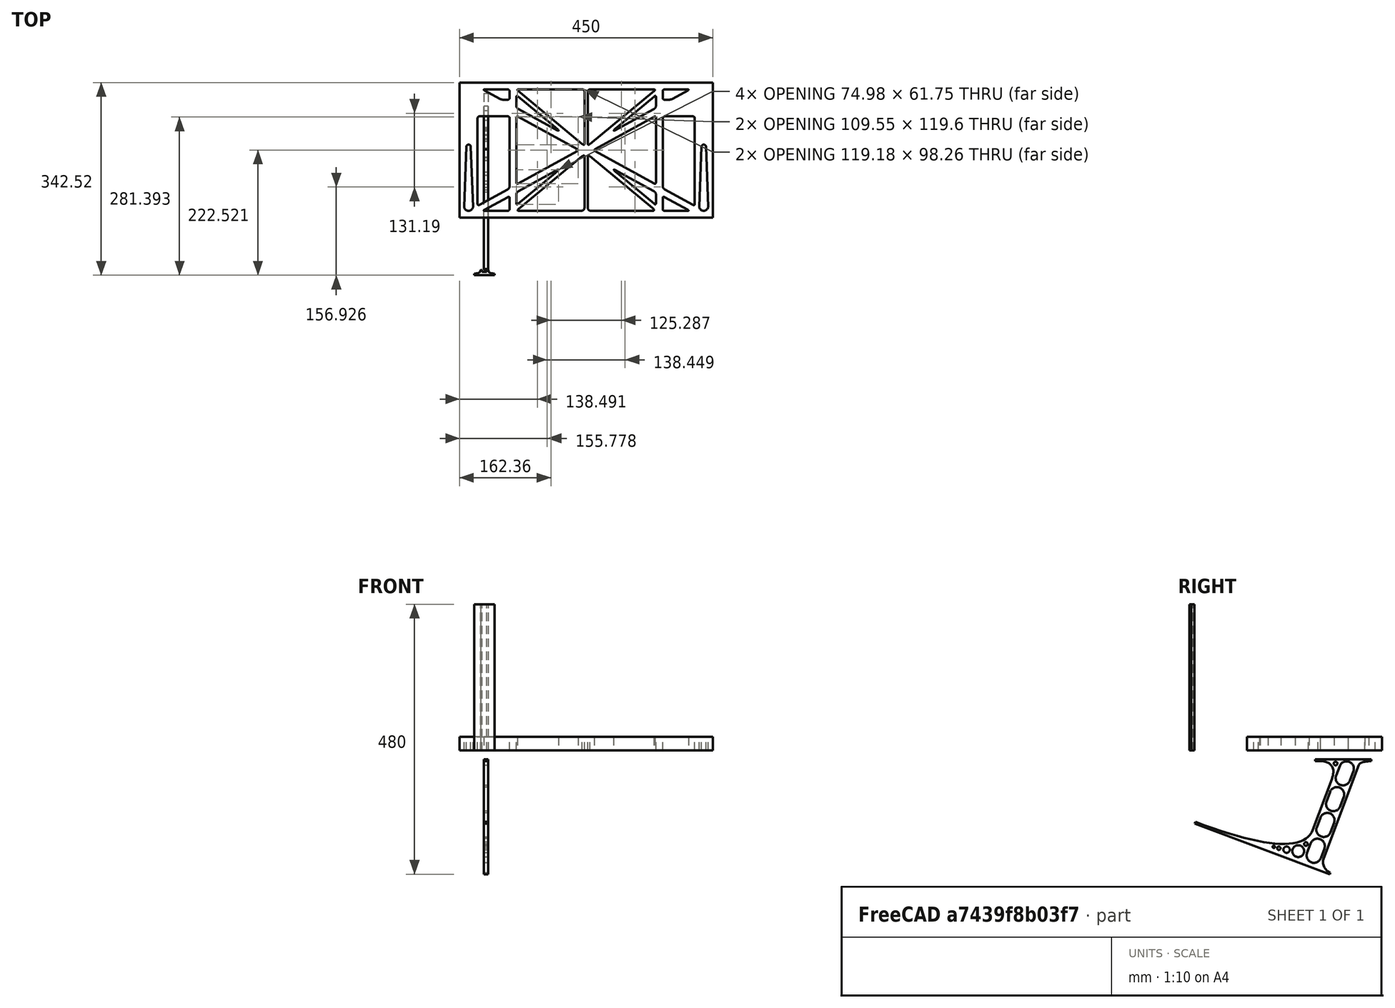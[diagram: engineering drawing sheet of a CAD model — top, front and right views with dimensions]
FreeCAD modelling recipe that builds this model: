
FCSTD DOCUMENT  (FreeCAD 0.19R0.19.2)
Label: laptopStand160FCStd
License: All rights reserved
LicenseURL: http://en.wikipedia.org/wiki/All_rights_reserved
objects: Sketcher::SketchObject×4, Part::Extrusion×3
note: 7 computed .brp shape members not serialized (recipe doc carries the construction recipe); baked Part::Feature solids carry a one-line shape summary decoded from their .brp

FEATURE [Sketcher::SketchObject] Sketch
  FullyConstrained = false
  sketch-geometry (349):
    g0: LineSegment StartX=-10.9272 StartY=-82.7794 StartZ=0 EndX=46.0728 EndY=-51.4823 EndZ=0
    g1: LineSegment StartX=-10.9272 StartY=76.4095 StartZ=0 EndX=-10.9272 EndY=-82.7794 EndZ=0
    g2: LineSegment StartX=46.0728 StartY=76.4095 StartZ=0 EndX=46.0728 EndY=-51.4823 EndZ=0
    g3: LineSegment StartX=-42.9272 StartY=136.221 StartZ=0 EndX=-42.9272 EndY=-103.779 EndZ=0
    g4: LineSegment StartX=407.073 StartY=136.221 StartZ=0 EndX=407.073 EndY=-103.779 EndZ=0
    g5: ArcOfCircle CenterX=-26.9272 CenterY=-83.7794 CenterZ=0 NormalX=0 NormalY=0 NormalZ=1 AngleXU=0 Radius=8 StartAngle=3.14159 EndAngle=6.28319
    g6: ArcOfCircle CenterX=391.073 CenterY=22.1087 CenterZ=0 NormalX=0 NormalY=0 NormalZ=1 AngleXU=0 Radius=8 StartAngle=-4.4e-15 EndAngle=3.14159
    g7: LineSegment StartX=399.073 StartY=22.1087 StartZ=0 EndX=399.073 EndY=-83.7794 EndZ=0
    g8: LineSegment StartX=383.073 StartY=22.1087 StartZ=0 EndX=383.073 EndY=-83.7794 EndZ=0
    g9: ArcOfCircle CenterX=391.073 CenterY=-83.7794 CenterZ=0 NormalX=0 NormalY=0 NormalZ=1 AngleXU=0 Radius=8 StartAngle=3.14159 EndAngle=6.28319
    g10: Circle CenterX=175.022 CenterY=27.0628 CenterZ=0 NormalX=0 NormalY=0 NormalZ=1 AngleXU=0 Radius=1
    g11: Circle CenterX=179.022 CenterY=24.8665 CenterZ=0 NormalX=0 NormalY=0 NormalZ=1 AngleXU=0 Radius=1
    g12: Circle CenterX=179.022 CenterY=27.0628 CenterZ=0 NormalX=0 NormalY=0 NormalZ=1 AngleXU=0 Radius=1
    g13: BSplineCurve PolesCount=3 KnotsCount=2 Degree=2 IsPeriodic=0
    g14: GeomPoint X=175.022 Y=27.0628 Z=0
    g15: GeomPoint X=179.022 Y=27.0628 Z=0
    g16: Circle CenterX=189.124 CenterY=27.0628 CenterZ=0 NormalX=0 NormalY=0 NormalZ=1 AngleXU=0 Radius=1
    g17: Circle CenterX=185.124 CenterY=24.8665 CenterZ=0 NormalX=0 NormalY=0 NormalZ=1 AngleXU=0 Radius=1
    g18: Circle CenterX=185.124 CenterY=27.0628 CenterZ=0 NormalX=0 NormalY=0 NormalZ=1 AngleXU=0 Radius=1
    g19: BSplineCurve PolesCount=3 KnotsCount=2 Degree=2 IsPeriodic=0
    g20: GeomPoint X=189.124 Y=27.0628 Z=0
    g21: GeomPoint X=185.124 Y=27.0628 Z=0
    g22: Circle CenterX=175.022 CenterY=5.37834 CenterZ=0 NormalX=0 NormalY=0 NormalZ=1 AngleXU=0 Radius=1
    g23: Circle CenterX=179.022 CenterY=7.57463 CenterZ=0 NormalX=0 NormalY=0 NormalZ=1 AngleXU=0 Radius=1
    g24: Circle CenterX=179.022 CenterY=5.34704 CenterZ=0 NormalX=0 NormalY=0 NormalZ=1 AngleXU=0 Radius=1
    g25: BSplineCurve PolesCount=3 KnotsCount=2 Degree=2 IsPeriodic=0
    g26: GeomPoint X=175.022 Y=5.37834 Z=0
    g27: GeomPoint X=179.022 Y=5.34704 Z=0
    g28: Circle CenterX=189.124 CenterY=5.37834 CenterZ=0 NormalX=0 NormalY=0 NormalZ=1 AngleXU=0 Radius=1
    g29: Circle CenterX=185.124 CenterY=7.57463 CenterZ=0 NormalX=0 NormalY=0 NormalZ=1 AngleXU=0 Radius=1
    g30: Circle CenterX=185.124 CenterY=5.34704 CenterZ=0 NormalX=0 NormalY=0 NormalZ=1 AngleXU=0 Radius=1
    g31: BSplineCurve PolesCount=3 KnotsCount=2 Degree=2 IsPeriodic=0
    g32: GeomPoint X=189.124 Y=5.37834 Z=0
    g33: GeomPoint X=185.124 Y=5.34704 Z=0
    g34: Circle CenterX=165.871 CenterY=18.1458 CenterZ=0 NormalX=0 NormalY=0 NormalZ=1 AngleXU=0 Radius=1
    g35: Circle CenterX=169.377 CenterY=16.2206 CenterZ=0 NormalX=0 NormalY=0 NormalZ=1 AngleXU=0 Radius=1
    g36: Circle CenterX=165.871 CenterY=14.2954 CenterZ=0 NormalX=0 NormalY=0 NormalZ=1 AngleXU=0 Radius=1
    g37: BSplineCurve PolesCount=3 KnotsCount=2 Degree=2 IsPeriodic=0
    g38: GeomPoint X=165.871 Y=18.1458 Z=0
    g39: GeomPoint X=165.871 Y=14.2954 Z=0
    g40: Circle CenterX=198.275 CenterY=18.1458 CenterZ=0 NormalX=0 NormalY=0 NormalZ=1 AngleXU=0 Radius=1
    g41: Circle CenterX=194.768 CenterY=16.2206 CenterZ=0 NormalX=0 NormalY=0 NormalZ=1 AngleXU=0 Radius=1
    g42: Circle CenterX=198.275 CenterY=14.2954 CenterZ=0 NormalX=0 NormalY=0 NormalZ=1 AngleXU=0 Radius=1
    g43: BSplineCurve PolesCount=3 KnotsCount=2 Degree=2 IsPeriodic=0
    g44: GeomPoint X=198.275 Y=18.1458 Z=0
    g45: GeomPoint X=198.275 Y=14.2954 Z=0
    g46: LineSegment StartX=407.073 StartY=-103.779 StartZ=0 EndX=-42.9272 EndY=-103.779 EndZ=0
    g47: LineSegment StartX=407.073 StartY=136.221 StartZ=0 EndX=-42.9272 EndY=136.221 EndZ=0
    g48: LineSegment StartX=46.0728 StartY=76.4095 StartZ=0 EndX=-10.9272 EndY=76.4095 EndZ=0
    g49: Circle CenterX=125.607 CenterY=54.1951 CenterZ=0 NormalX=0 NormalY=0 NormalZ=1 AngleXU=0 Radius=1
    g50: Circle CenterX=139.632 CenterY=46.4944 CenterZ=0 NormalX=0 NormalY=0 NormalZ=1 AngleXU=0 Radius=1
    g51: Circle CenterX=127.326 CenterY=56.7187 CenterZ=0 NormalX=0 NormalY=0 NormalZ=1 AngleXU=0 Radius=1
    g52: BSplineCurve PolesCount=3 KnotsCount=2 Degree=2 IsPeriodic=0
    g53: GeomPoint X=125.607 Y=54.1951 Z=0
    g54: GeomPoint X=127.326 Y=56.7187 Z=0
    g55: Circle CenterX=236.821 CenterY=56.7187 CenterZ=0 NormalX=0 NormalY=0 NormalZ=1 AngleXU=0 Radius=1
    g56: Circle CenterX=224.513 CenterY=46.4944 CenterZ=0 NormalX=0 NormalY=0 NormalZ=1 AngleXU=0 Radius=1
    g57: Circle CenterX=238.538 CenterY=54.1951 CenterZ=0 NormalX=0 NormalY=0 NormalZ=1 AngleXU=0 Radius=1
    g58: BSplineCurve PolesCount=3 KnotsCount=2 Degree=2 IsPeriodic=0
    g59: GeomPoint X=236.821 Y=56.7187 Z=0
    g60: GeomPoint X=238.538 Y=54.1951 Z=0
    g61: Circle CenterX=238.538 CenterY=-21.7539 CenterZ=0 NormalX=0 NormalY=0 NormalZ=1 AngleXU=0 Radius=1
    g62: Circle CenterX=224.513 CenterY=-14.0532 CenterZ=0 NormalX=0 NormalY=0 NormalZ=1 AngleXU=0 Radius=1
    g63: Circle CenterX=236.821 CenterY=-24.2775 CenterZ=0 NormalX=0 NormalY=0 NormalZ=1 AngleXU=0 Radius=1
    g64: BSplineCurve PolesCount=3 KnotsCount=2 Degree=2 IsPeriodic=0
    g65: GeomPoint X=238.538 Y=-21.7539 Z=0
    g66: GeomPoint X=236.821 Y=-24.2775 Z=0
    g67: Circle CenterX=125.607 CenterY=-21.7539 CenterZ=0 NormalX=0 NormalY=0 NormalZ=1 AngleXU=0 Radius=1
    g68: Circle CenterX=139.632 CenterY=-14.0532 CenterZ=0 NormalX=0 NormalY=0 NormalZ=1 AngleXU=0 Radius=1
    g69: Circle CenterX=127.325 CenterY=-24.2775 CenterZ=0 NormalX=0 NormalY=0 NormalZ=1 AngleXU=0 Radius=1
    g70: BSplineCurve PolesCount=3 KnotsCount=2 Degree=2 IsPeriodic=0
    g71: GeomPoint X=125.607 Y=-21.7539 Z=0
    g72: GeomPoint X=127.325 Y=-24.2775 Z=0
    g73: Circle CenterX=302.996 CenterY=111.695 CenterZ=0 NormalX=0 NormalY=0 NormalZ=1 AngleXU=0 Radius=1
    g74: Circle CenterX=306.073 CenterY=114.251 CenterZ=0 NormalX=0 NormalY=0 NormalZ=1 AngleXU=0 Radius=1
    g75: Circle CenterX=306.073 CenterY=110.251 CenterZ=0 NormalX=0 NormalY=0 NormalZ=1 AngleXU=0 Radius=1
    g76: BSplineCurve PolesCount=3 KnotsCount=2 Degree=2 IsPeriodic=0
    g77: GeomPoint X=302.996 Y=111.695 Z=0
    g78: GeomPoint X=306.073 Y=110.251 Z=0
    g79: Circle CenterX=306.073 CenterY=95.2763 CenterZ=0 NormalX=0 NormalY=0 NormalZ=1 AngleXU=0 Radius=1
    g80: Circle CenterX=306.073 CenterY=91.2763 CenterZ=0 NormalX=0 NormalY=0 NormalZ=1 AngleXU=0 Radius=1
    g81: Circle CenterX=302.567 CenterY=89.3511 CenterZ=0 NormalX=0 NormalY=0 NormalZ=1 AngleXU=0 Radius=1
    g82: BSplineCurve PolesCount=3 KnotsCount=2 Degree=2 IsPeriodic=0
    g83: GeomPoint X=306.073 Y=95.2763 Z=0
    g84: GeomPoint X=302.567 Y=89.3511 Z=0
    g85: LineSegment StartX=306.073 StartY=110.251 StartZ=0 EndX=306.073 EndY=95.2763 EndZ=0
    g86: LineSegment StartX=302.996 StartY=111.695 StartZ=0 EndX=236.821 EndY=56.7187 EndZ=0
    g87: LineSegment StartX=238.538 StartY=54.1951 StartZ=0 EndX=302.567 EndY=89.3511 EndZ=0
    g88: Circle CenterX=61.1496 CenterY=111.695 CenterZ=0 NormalX=0 NormalY=0 NormalZ=1 AngleXU=0 Radius=1
    g89: Circle CenterX=58.0728 CenterY=114.251 CenterZ=0 NormalX=0 NormalY=0 NormalZ=1 AngleXU=0 Radius=1
    g90: Circle CenterX=58.0728 CenterY=110.251 CenterZ=0 NormalX=0 NormalY=0 NormalZ=1 AngleXU=0 Radius=1
    g91: BSplineCurve PolesCount=3 KnotsCount=2 Degree=2 IsPeriodic=0
    g92: GeomPoint X=61.1496 Y=111.695 Z=0
    g93: GeomPoint X=58.0728 Y=110.251 Z=0
    g94: Circle CenterX=61.5791 CenterY=89.3511 CenterZ=0 NormalX=0 NormalY=0 NormalZ=1 AngleXU=0 Radius=1
    g95: Circle CenterX=58.0728 CenterY=91.2763 CenterZ=0 NormalX=0 NormalY=0 NormalZ=1 AngleXU=0 Radius=1
    g96: Circle CenterX=58.0728 CenterY=95.2763 CenterZ=0 NormalX=0 NormalY=0 NormalZ=1 AngleXU=0 Radius=1
    g97: BSplineCurve PolesCount=3 KnotsCount=2 Degree=2 IsPeriodic=0
    g98: GeomPoint X=61.5791 Y=89.3511 Z=0
    g99: GeomPoint X=58.0728 Y=95.2763 Z=0
    g100: LineSegment StartX=58.0728 StartY=110.251 StartZ=0 EndX=58.0728 EndY=95.2763 EndZ=0
    g101: LineSegment StartX=61.1496 StartY=111.695 StartZ=0 EndX=127.326 EndY=56.7187 EndZ=0
    g102: LineSegment StartX=125.607 StartY=54.1951 StartZ=0 EndX=61.5791 EndY=89.3511 EndZ=0
    g103: Circle CenterX=61.5791 CenterY=-56.9099 CenterZ=0 NormalX=0 NormalY=0 NormalZ=1 AngleXU=0 Radius=1
    g104: Circle CenterX=58.0728 CenterY=-58.8351 CenterZ=0 NormalX=0 NormalY=0 NormalZ=1 AngleXU=0 Radius=1
    g105: Circle CenterX=58.0728 CenterY=-62.8351 CenterZ=0 NormalX=0 NormalY=0 NormalZ=1 AngleXU=0 Radius=1
    g106: BSplineCurve PolesCount=3 KnotsCount=2 Degree=2 IsPeriodic=0
    g107: GeomPoint X=61.5791 Y=-56.9099 Z=0
    g108: GeomPoint X=58.0728 Y=-62.8351 Z=0
    g109: Circle CenterX=58.0728 CenterY=-77.8102 CenterZ=0 NormalX=0 NormalY=0 NormalZ=1 AngleXU=0 Radius=1
    g110: Circle CenterX=58.0728 CenterY=-81.8102 CenterZ=0 NormalX=0 NormalY=0 NormalZ=1 AngleXU=0 Radius=1
    g111: Circle CenterX=61.1496 CenterY=-79.2541 CenterZ=0 NormalX=0 NormalY=0 NormalZ=1 AngleXU=0 Radius=1
    g112: BSplineCurve PolesCount=3 KnotsCount=2 Degree=2 IsPeriodic=0
    g113: GeomPoint X=58.0728 Y=-77.8102 Z=0
    g114: GeomPoint X=61.1496 Y=-79.2541 Z=0
    g115: LineSegment StartX=58.0728 StartY=-62.8351 StartZ=0 EndX=58.0728 EndY=-77.8102 EndZ=0
    g116: LineSegment StartX=61.1496 StartY=-79.2541 StartZ=0 EndX=127.325 EndY=-24.2775 EndZ=0
    g117: LineSegment StartX=125.607 StartY=-21.7539 StartZ=0 EndX=61.5791 EndY=-56.9099 EndZ=0
    g118: Circle CenterX=302.567 CenterY=-56.9099 CenterZ=0 NormalX=0 NormalY=0 NormalZ=1 AngleXU=0 Radius=1
    g119: Circle CenterX=306.073 CenterY=-58.8351 CenterZ=0 NormalX=0 NormalY=0 NormalZ=1 AngleXU=0 Radius=1
    g120: Circle CenterX=306.073 CenterY=-62.8351 CenterZ=0 NormalX=0 NormalY=0 NormalZ=1 AngleXU=0 Radius=1
    g121: BSplineCurve PolesCount=3 KnotsCount=2 Degree=2 IsPeriodic=0
    g122: GeomPoint X=302.567 Y=-56.9099 Z=0
    g123: GeomPoint X=306.073 Y=-62.8351 Z=0
    g124: Circle CenterX=302.996 CenterY=-79.2541 CenterZ=0 NormalX=0 NormalY=0 NormalZ=1 AngleXU=0 Radius=1
    g125: Circle CenterX=306.073 CenterY=-81.8102 CenterZ=0 NormalX=0 NormalY=0 NormalZ=1 AngleXU=0 Radius=1
    g126: Circle CenterX=306.073 CenterY=-77.8102 CenterZ=0 NormalX=0 NormalY=0 NormalZ=1 AngleXU=0 Radius=1
    g127: BSplineCurve PolesCount=3 KnotsCount=2 Degree=2 IsPeriodic=0
    g128: GeomPoint X=302.996 Y=-79.2541 Z=0
    g129: GeomPoint X=306.073 Y=-77.8102 Z=0
    g130: LineSegment StartX=306.073 StartY=-62.8351 StartZ=0 EndX=306.073 EndY=-77.8102 EndZ=0
    g131: LineSegment StartX=302.996 StartY=-79.2541 StartZ=0 EndX=236.821 EndY=-24.2775 EndZ=0
    g132: LineSegment StartX=238.538 StartY=-21.7539 StartZ=0 EndX=302.567 EndY=-56.9099 EndZ=0
    g133: Circle CenterX=61.6457 CenterY=-88.8112 CenterZ=0 NormalX=0 NormalY=0 NormalZ=1 AngleXU=0 Radius=1
    g134: Circle CenterX=58.0728 CenterY=-91.7794 CenterZ=0 NormalX=0 NormalY=0 NormalZ=1 AngleXU=0 Radius=1
    g135: Circle CenterX=63.9135 CenterY=-91.7794 CenterZ=0 NormalX=0 NormalY=0 NormalZ=1 AngleXU=0 Radius=1
    g136: BSplineCurve PolesCount=3 KnotsCount=2 Degree=2 IsPeriodic=0
    g137: GeomPoint X=61.6457 Y=-88.8112 Z=0
    g138: GeomPoint X=63.9135 Y=-91.7794 Z=0
    g139: Circle CenterX=179.022 CenterY=-85.8163 CenterZ=0 NormalX=0 NormalY=0 NormalZ=1 AngleXU=0 Radius=1
    g140: Circle CenterX=179.022 CenterY=-91.7794 CenterZ=0 NormalX=0 NormalY=0 NormalZ=1 AngleXU=0 Radius=1
    g141: Circle CenterX=171.895 CenterY=-91.7794 CenterZ=0 NormalX=0 NormalY=0 NormalZ=1 AngleXU=0 Radius=1
    g142: BSplineCurve PolesCount=3 KnotsCount=2 Degree=2 IsPeriodic=0
    g143: GeomPoint X=179.022 Y=-85.8163 Z=0
    g144: GeomPoint X=171.895 Y=-91.7794 Z=0
    g145: Circle CenterX=185.124 CenterY=-86.2028 CenterZ=0 NormalX=0 NormalY=0 NormalZ=1 AngleXU=0 Radius=1
    g146: Circle CenterX=185.124 CenterY=-91.7794 CenterZ=0 NormalX=0 NormalY=0 NormalZ=1 AngleXU=0 Radius=1
    g147: Circle CenterX=191.747 CenterY=-91.7794 CenterZ=0 NormalX=0 NormalY=0 NormalZ=1 AngleXU=0 Radius=1
    g148: BSplineCurve PolesCount=3 KnotsCount=2 Degree=2 IsPeriodic=0
    g149: GeomPoint X=185.124 Y=-86.2028 Z=0
    g150: GeomPoint X=191.747 Y=-91.7794 Z=0
    g151: Circle CenterX=299.888 CenterY=-86.6413 CenterZ=0 NormalX=0 NormalY=0 NormalZ=1 AngleXU=0 Radius=1
    g152: Circle CenterX=306.073 CenterY=-91.7794 CenterZ=0 NormalX=0 NormalY=0 NormalZ=1 AngleXU=0 Radius=1
    g153: Circle CenterX=298.776 CenterY=-91.7794 CenterZ=0 NormalX=0 NormalY=0 NormalZ=1 AngleXU=0 Radius=1
    g154: BSplineCurve PolesCount=3 KnotsCount=2 Degree=2 IsPeriodic=0
    g155: GeomPoint X=299.888 Y=-86.6413 Z=0
    g156: GeomPoint X=298.776 Y=-91.7794 Z=0
    g157: LineSegment StartX=189.124 StartY=5.37834 StartZ=0 EndX=299.888 EndY=-86.6413 EndZ=0
    g158: LineSegment StartX=298.776 StartY=-91.7794 StartZ=0 EndX=191.747 EndY=-91.7794 EndZ=0
    g159: LineSegment StartX=185.124 StartY=-86.2028 StartZ=0 EndX=185.124 EndY=5.34704 EndZ=0
    g160: LineSegment StartX=179.022 StartY=5.34704 StartZ=0 EndX=179.022 EndY=-85.8163 EndZ=0
    g161: LineSegment StartX=171.895 StartY=-91.7794 StartZ=0 EndX=63.9135 EndY=-91.7794 EndZ=0
    g162: LineSegment StartX=61.6457 StartY=-88.8112 StartZ=0 EndX=175.022 EndY=5.37834 EndZ=0
    g163: Circle CenterX=302.073 CenterY=124.221 CenterZ=0 NormalX=0 NormalY=0 NormalZ=1 AngleXU=0 Radius=1
    g164: Circle CenterX=306.073 CenterY=124.221 CenterZ=0 NormalX=0 NormalY=0 NormalZ=1 AngleXU=0 Radius=1
    g165: Circle CenterX=302.996 CenterY=121.665 CenterZ=0 NormalX=0 NormalY=0 NormalZ=1 AngleXU=0 Radius=1
    g166: BSplineCurve PolesCount=3 KnotsCount=2 Degree=2 IsPeriodic=0
    g167: GeomPoint X=302.073 Y=124.221 Z=0
    g168: GeomPoint X=302.996 Y=121.665 Z=0
    g169: Circle CenterX=189.124 CenterY=124.221 CenterZ=0 NormalX=0 NormalY=0 NormalZ=1 AngleXU=0 Radius=1
    g170: Circle CenterX=185.124 CenterY=124.221 CenterZ=0 NormalX=0 NormalY=0 NormalZ=1 AngleXU=0 Radius=1
    g171: Circle CenterX=185.124 CenterY=120.221 CenterZ=0 NormalX=0 NormalY=0 NormalZ=1 AngleXU=0 Radius=1
    g172: BSplineCurve PolesCount=3 KnotsCount=2 Degree=2 IsPeriodic=0
    g173: GeomPoint X=189.124 Y=124.221 Z=0
    g174: GeomPoint X=185.124 Y=120.221 Z=0
    g175: Circle CenterX=175.022 CenterY=124.221 CenterZ=0 NormalX=0 NormalY=0 NormalZ=1 AngleXU=0 Radius=1
    g176: Circle CenterX=179.022 CenterY=124.221 CenterZ=0 NormalX=0 NormalY=0 NormalZ=1 AngleXU=0 Radius=1
    g177: Circle CenterX=179.022 CenterY=120.221 CenterZ=0 NormalX=0 NormalY=0 NormalZ=1 AngleXU=0 Radius=1
    g178: BSplineCurve PolesCount=3 KnotsCount=2 Degree=2 IsPeriodic=0
    g179: GeomPoint X=175.022 Y=124.221 Z=0
    g180: GeomPoint X=179.022 Y=120.221 Z=0
    g181: Circle CenterX=62.0728 CenterY=124.221 CenterZ=0 NormalX=0 NormalY=0 NormalZ=1 AngleXU=0 Radius=1
    g182: Circle CenterX=58.0728 CenterY=124.221 CenterZ=0 NormalX=0 NormalY=0 NormalZ=1 AngleXU=0 Radius=1
    g183: Circle CenterX=61.1496 CenterY=121.665 CenterZ=0 NormalX=0 NormalY=0 NormalZ=1 AngleXU=0 Radius=1
    g184: BSplineCurve PolesCount=3 KnotsCount=2 Degree=2 IsPeriodic=0
    g185: GeomPoint X=62.0728 Y=124.221 Z=0
    g186: GeomPoint X=61.1496 Y=121.665 Z=0
    g187: LineSegment StartX=62.0728 StartY=124.221 StartZ=0 EndX=175.022 EndY=124.221 EndZ=0
    g188: LineSegment StartX=179.022 StartY=120.221 StartZ=0 EndX=179.022 EndY=27.0628 EndZ=0
    g189: LineSegment StartX=185.124 StartY=27.0628 StartZ=0 EndX=185.124 EndY=120.221 EndZ=0
    g190: LineSegment StartX=189.124 StartY=124.221 StartZ=0 EndX=302.073 EndY=124.221 EndZ=0
    g191: LineSegment StartX=302.996 StartY=121.665 StartZ=0 EndX=189.124 EndY=27.0628 EndZ=0
    g192: LineSegment StartX=175.022 StartY=27.0628 StartZ=0 EndX=61.1496 EndY=121.665 EndZ=0
    g193: Circle CenterX=61.5791 CenterY=75.4095 CenterZ=0 NormalX=0 NormalY=0 NormalZ=1 AngleXU=0 Radius=1
    g194: Circle CenterX=58.0728 CenterY=77.3346 CenterZ=0 NormalX=0 NormalY=0 NormalZ=1 AngleXU=0 Radius=1
    g195: Circle CenterX=58.0728 CenterY=73.3346 CenterZ=0 NormalX=0 NormalY=0 NormalZ=1 AngleXU=0 Radius=1
    g196: BSplineCurve PolesCount=3 KnotsCount=2 Degree=2 IsPeriodic=0
    g197: GeomPoint X=61.5791 Y=75.4095 Z=0
    g198: GeomPoint X=58.0728 Y=73.3346 Z=0
    g199: Circle CenterX=58.0728 CenterY=-40.8935 CenterZ=0 NormalX=0 NormalY=0 NormalZ=1 AngleXU=0 Radius=1
    g200: Circle CenterX=58.0728 CenterY=-44.8935 CenterZ=0 NormalX=0 NormalY=0 NormalZ=1 AngleXU=0 Radius=1
    g201: Circle CenterX=61.5791 CenterY=-42.9683 CenterZ=0 NormalX=0 NormalY=0 NormalZ=1 AngleXU=0 Radius=1
    g202: BSplineCurve PolesCount=3 KnotsCount=2 Degree=2 IsPeriodic=0
    g203: GeomPoint X=58.0728 Y=-40.8935 Z=0
    g204: GeomPoint X=61.5791 Y=-42.9683 Z=0
    g205: LineSegment StartX=61.5791 StartY=-42.9683 StartZ=0 EndX=165.871 EndY=14.2954 EndZ=0
    g206: LineSegment StartX=165.871 StartY=18.1458 StartZ=0 EndX=61.5791 EndY=75.4095 EndZ=0
    g207: LineSegment StartX=58.0728 StartY=73.3346 StartZ=0 EndX=58.0728 EndY=-40.8935 EndZ=0
    g208: Circle CenterX=302.567 CenterY=-42.9683 CenterZ=0 NormalX=0 NormalY=0 NormalZ=1 AngleXU=0 Radius=1
    g209: Circle CenterX=306.073 CenterY=-44.8935 CenterZ=0 NormalX=0 NormalY=0 NormalZ=1 AngleXU=0 Radius=1
    g210: Circle CenterX=306.073 CenterY=-40.8935 CenterZ=0 NormalX=0 NormalY=0 NormalZ=1 AngleXU=0 Radius=1
    g211: BSplineCurve PolesCount=3 KnotsCount=2 Degree=2 IsPeriodic=0
    g212: GeomPoint X=302.567 Y=-42.9683 Z=0
    g213: GeomPoint X=306.073 Y=-40.8935 Z=0
    g214: Circle CenterX=306.073 CenterY=73.3346 CenterZ=0 NormalX=0 NormalY=0 NormalZ=1 AngleXU=0 Radius=1
    g215: Circle CenterX=306.073 CenterY=77.3346 CenterZ=0 NormalX=0 NormalY=0 NormalZ=1 AngleXU=0 Radius=1
    g216: Circle CenterX=302.567 CenterY=75.4095 CenterZ=0 NormalX=0 NormalY=0 NormalZ=1 AngleXU=0 Radius=1
    g217: BSplineCurve PolesCount=3 KnotsCount=2 Degree=2 IsPeriodic=0
    g218: GeomPoint X=306.073 Y=73.3346 Z=0
    g219: GeomPoint X=302.567 Y=75.4095 Z=0
    g220: LineSegment StartX=302.567 StartY=-42.9683 StartZ=0 EndX=198.275 EndY=14.2954 EndZ=0
    g221: LineSegment StartX=198.275 StartY=18.1458 StartZ=0 EndX=302.567 EndY=75.4095 EndZ=0
    g222: LineSegment StartX=306.073 StartY=73.3346 StartZ=0 EndX=306.073 EndY=-40.8935 EndZ=0
    g223: LineSegment StartX=322.073 StartY=105.865 StartZ=0 EndX=328.643 EndY=105.865 EndZ=0
    g224: LineSegment StartX=318.073 StartY=120.221 StartZ=0 EndX=318.073 EndY=109.865 EndZ=0
    g225: LineSegment StartX=336.157 StartY=107.779 StartZ=0 EndX=362.567 EndY=122.294 EndZ=0
    g226: Circle CenterX=362.073 CenterY=124.221 CenterZ=0 NormalX=0 NormalY=0 NormalZ=1 AngleXU=0 Radius=1
    g227: Circle CenterX=366.073 CenterY=124.221 CenterZ=0 NormalX=0 NormalY=0 NormalZ=1 AngleXU=0 Radius=1
    g228: Circle CenterX=362.567 CenterY=122.294 CenterZ=0 NormalX=0 NormalY=0 NormalZ=1 AngleXU=0 Radius=1
    g229: BSplineCurve PolesCount=3 KnotsCount=2 Degree=2 IsPeriodic=0
    g230: GeomPoint X=362.073 Y=124.221 Z=0
    g231: GeomPoint X=362.567 Y=122.294 Z=0
    g232: Circle CenterX=322.073 CenterY=124.221 CenterZ=0 NormalX=0 NormalY=0 NormalZ=1 AngleXU=0 Radius=1
    g233: Circle CenterX=318.073 CenterY=124.221 CenterZ=0 NormalX=0 NormalY=0 NormalZ=1 AngleXU=0 Radius=1
    g234: Circle CenterX=318.073 CenterY=120.221 CenterZ=0 NormalX=0 NormalY=0 NormalZ=1 AngleXU=0 Radius=1
    g235: BSplineCurve PolesCount=3 KnotsCount=2 Degree=2 IsPeriodic=0
    g236: GeomPoint X=322.073 Y=124.221 Z=0
    g237: GeomPoint X=318.073 Y=120.221 Z=0
    g238: Circle CenterX=322.073 CenterY=105.865 CenterZ=0 NormalX=0 NormalY=0 NormalZ=1 AngleXU=0 Radius=1
    g239: Circle CenterX=318.073 CenterY=105.865 CenterZ=0 NormalX=0 NormalY=0 NormalZ=1 AngleXU=0 Radius=1
    g240: Circle CenterX=318.073 CenterY=109.865 CenterZ=0 NormalX=0 NormalY=0 NormalZ=1 AngleXU=0 Radius=1
    g241: BSplineCurve PolesCount=3 KnotsCount=2 Degree=2 IsPeriodic=0
    g242: GeomPoint X=322.073 Y=105.865 Z=0
    g243: GeomPoint X=318.073 Y=109.865 Z=0
    g244: Circle CenterX=336.157 CenterY=107.779 CenterZ=0 NormalX=0 NormalY=0 NormalZ=1 AngleXU=0 Radius=1
    g245: Circle CenterX=332.651 CenterY=105.853 CenterZ=0 NormalX=0 NormalY=0 NormalZ=1 AngleXU=0 Radius=1
    g246: Circle CenterX=328.643 CenterY=105.865 CenterZ=0 NormalX=0 NormalY=0 NormalZ=1 AngleXU=0 Radius=1
    g247: BSplineCurve PolesCount=3 KnotsCount=2 Degree=2 IsPeriodic=0
    g248: GeomPoint X=336.157 Y=107.779 Z=0
    g249: GeomPoint X=328.643 Y=105.865 Z=0
    g250: LineSegment StartX=322.073 StartY=124.221 StartZ=0 EndX=362.073 EndY=124.221 EndZ=0
    g251: Circle CenterX=371.567 CenterY=-80.8644 CenterZ=0 NormalX=0 NormalY=0 NormalZ=1 AngleXU=0 Radius=1
    g252: Circle CenterX=375.073 CenterY=-82.7896 CenterZ=0 NormalX=0 NormalY=0 NormalZ=1 AngleXU=0 Radius=1
    g253: Circle CenterX=375.073 CenterY=-78.7896 CenterZ=0 NormalX=0 NormalY=0 NormalZ=1 AngleXU=0 Radius=1
    g254: BSplineCurve PolesCount=3 KnotsCount=2 Degree=2 IsPeriodic=0
    g255: GeomPoint X=371.567 Y=-80.8644 Z=0
    g256: GeomPoint X=375.073 Y=-78.7896 Z=0
    g257: Circle CenterX=321.579 CenterY=-53.4075 CenterZ=0 NormalX=0 NormalY=0 NormalZ=1 AngleXU=0 Radius=1
    g258: Circle CenterX=318.073 CenterY=-51.4823 CenterZ=0 NormalX=0 NormalY=0 NormalZ=1 AngleXU=0 Radius=1
    g259: Circle CenterX=318.073 CenterY=-47.4805 CenterZ=0 NormalX=0 NormalY=0 NormalZ=1 AngleXU=0 Radius=1
    g260: BSplineCurve PolesCount=3 KnotsCount=2 Degree=2 IsPeriodic=0
    g261: GeomPoint X=321.579 Y=-53.4075 Z=0
    g262: GeomPoint X=318.073 Y=-47.4805 Z=0
    g263: LineSegment StartX=371.567 StartY=-80.8644 StartZ=0 EndX=321.579 EndY=-53.4075 EndZ=0
    g264: Circle CenterX=321.579 CenterY=-67.3492 CenterZ=0 NormalX=0 NormalY=0 NormalZ=1 AngleXU=0 Radius=1
    g265: Circle CenterX=318.073 CenterY=-65.424 CenterZ=0 NormalX=0 NormalY=0 NormalZ=1 AngleXU=0 Radius=1
    g266: Circle CenterX=318.073 CenterY=-69.424 CenterZ=0 NormalX=0 NormalY=0 NormalZ=1 AngleXU=0 Radius=1
    g267: BSplineCurve PolesCount=3 KnotsCount=2 Degree=2 IsPeriodic=0
    g268: GeomPoint X=321.579 Y=-67.3492 Z=0
    g269: GeomPoint X=318.073 Y=-69.424 Z=0
    g270: Circle CenterX=362.567 CenterY=-89.8542 CenterZ=0 NormalX=0 NormalY=0 NormalZ=1 AngleXU=0 Radius=1
    g271: Circle CenterX=366.073 CenterY=-91.7794 CenterZ=0 NormalX=0 NormalY=0 NormalZ=1 AngleXU=0 Radius=1
    g272: Circle CenterX=362.073 CenterY=-91.7794 CenterZ=0 NormalX=0 NormalY=0 NormalZ=1 AngleXU=0 Radius=1
    g273: BSplineCurve PolesCount=3 KnotsCount=2 Degree=2 IsPeriodic=0
    g274: GeomPoint X=362.567 Y=-89.8542 Z=0
    g275: GeomPoint X=362.073 Y=-91.7794 Z=0
    g276: Circle CenterX=322.073 CenterY=-91.7794 CenterZ=0 NormalX=0 NormalY=0 NormalZ=1 AngleXU=0 Radius=1
    g277: Circle CenterX=318.073 CenterY=-91.7794 CenterZ=0 NormalX=0 NormalY=0 NormalZ=1 AngleXU=0 Radius=1
    g278: Circle CenterX=318.073 CenterY=-87.7794 CenterZ=0 NormalX=0 NormalY=0 NormalZ=1 AngleXU=0 Radius=1
    g279: BSplineCurve PolesCount=3 KnotsCount=2 Degree=2 IsPeriodic=0
    g280: GeomPoint X=322.073 Y=-91.7794 Z=0
    g281: GeomPoint X=318.073 Y=-87.7794 Z=0
    g282: LineSegment StartX=362.567 StartY=-89.8542 StartZ=0 EndX=321.579 EndY=-67.3492 EndZ=0
    g283: LineSegment StartX=318.073 StartY=-69.424 StartZ=0 EndX=318.073 EndY=-87.7794 EndZ=0
    g284: LineSegment StartX=322.073 StartY=-91.7794 StartZ=0 EndX=362.073 EndY=-91.7794 EndZ=0
    g285: Circle CenterX=2.07281 CenterY=124.221 CenterZ=0 NormalX=0 NormalY=0 NormalZ=1 AngleXU=0 Radius=1
    g286: Circle CenterX=1.57905 CenterY=122.295 CenterZ=0 NormalX=0 NormalY=0 NormalZ=1 AngleXU=0 Radius=1
    g287: BSplineCurve PolesCount=3 KnotsCount=2 Degree=2 IsPeriodic=0
    g288: GeomPoint X=2.07281 Y=124.221 Z=0
    g289: GeomPoint X=1.57905 Y=122.295 Z=0
    g290: Circle CenterX=42.0728 CenterY=124.221 CenterZ=0 NormalX=0 NormalY=0 NormalZ=1 AngleXU=0 Radius=1
    g291: Circle CenterX=46.0728 CenterY=124.221 CenterZ=0 NormalX=0 NormalY=0 NormalZ=1 AngleXU=0 Radius=1
    g292: Circle CenterX=46.0728 CenterY=120.221 CenterZ=0 NormalX=0 NormalY=0 NormalZ=1 AngleXU=0 Radius=1
    g293: BSplineCurve PolesCount=3 KnotsCount=2 Degree=2 IsPeriodic=0
    g294: GeomPoint X=42.0728 Y=124.221 Z=0
    g295: GeomPoint X=46.0728 Y=120.221 Z=0
    g296: Circle CenterX=46.0728 CenterY=109.865 CenterZ=0 NormalX=0 NormalY=0 NormalZ=1 AngleXU=0 Radius=1
    g297: Circle CenterX=46.0728 CenterY=105.865 CenterZ=0 NormalX=0 NormalY=0 NormalZ=1 AngleXU=0 Radius=1
    g298: Circle CenterX=42.0728 CenterY=105.865 CenterZ=0 NormalX=0 NormalY=0 NormalZ=1 AngleXU=0 Radius=1
    g299: BSplineCurve PolesCount=3 KnotsCount=2 Degree=2 IsPeriodic=0
    g300: GeomPoint X=46.0728 Y=109.865 Z=0
    g301: GeomPoint X=42.0728 Y=105.865 Z=0
    g302: Circle CenterX=35.5028 CenterY=105.865 CenterZ=0 NormalX=0 NormalY=0 NormalZ=1 AngleXU=0 Radius=1
    g303: Circle CenterX=31.5028 CenterY=105.865 CenterZ=0 NormalX=0 NormalY=0 NormalZ=1 AngleXU=0 Radius=1
    g304: Circle CenterX=27.9965 CenterY=107.79 CenterZ=0 NormalX=0 NormalY=0 NormalZ=1 AngleXU=0 Radius=1
    g305: BSplineCurve PolesCount=3 KnotsCount=2 Degree=2 IsPeriodic=0
    g306: GeomPoint X=35.5028 Y=105.865 Z=0
    g307: GeomPoint X=27.9965 Y=107.79 Z=0
    g308: LineSegment StartX=2.07281 StartY=124.221 StartZ=0 EndX=42.0728 EndY=124.221 EndZ=0
    g309: LineSegment StartX=46.0728 StartY=120.221 StartZ=0 EndX=46.0728 EndY=109.865 EndZ=0
    g310: LineSegment StartX=42.0728 StartY=105.865 StartZ=0 EndX=35.5028 EndY=105.865 EndZ=0
    g311: LineSegment StartX=27.9965 StartY=107.79 StartZ=0 EndX=1.57905 EndY=122.295 EndZ=0
    g312: Circle CenterX=42.5666 CenterY=-67.3492 CenterZ=0 NormalX=0 NormalY=0 NormalZ=1 AngleXU=0 Radius=1
    g313: Circle CenterX=46.0728 CenterY=-65.424 CenterZ=0 NormalX=0 NormalY=0 NormalZ=1 AngleXU=0 Radius=1
    g314: Circle CenterX=46.0728 CenterY=-69.424 CenterZ=0 NormalX=0 NormalY=0 NormalZ=1 AngleXU=0 Radius=1
    g315: BSplineCurve PolesCount=3 KnotsCount=2 Degree=2 IsPeriodic=0
    g316: GeomPoint X=42.5666 Y=-67.3492 Z=0
    g317: GeomPoint X=46.0728 Y=-69.424 Z=0
    g318: Circle CenterX=46.0728 CenterY=-87.7794 CenterZ=0 NormalX=0 NormalY=0 NormalZ=1 AngleXU=0 Radius=1
    g319: Circle CenterX=46.0728 CenterY=-91.7794 CenterZ=0 NormalX=0 NormalY=0 NormalZ=1 AngleXU=0 Radius=1
    g320: Circle CenterX=42.0728 CenterY=-91.7794 CenterZ=0 NormalX=0 NormalY=0 NormalZ=1 AngleXU=0 Radius=1
    g321: BSplineCurve PolesCount=3 KnotsCount=2 Degree=2 IsPeriodic=0
    g322: GeomPoint X=46.0728 Y=-87.7794 Z=0
    g323: GeomPoint X=42.0728 Y=-91.7794 Z=0
    g324: Circle CenterX=2.07281 CenterY=-91.7794 CenterZ=0 NormalX=0 NormalY=0 NormalZ=1 AngleXU=0 Radius=1
    g325: Circle CenterX=-1.92719 CenterY=-91.7794 CenterZ=0 NormalX=0 NormalY=0 NormalZ=1 AngleXU=0 Radius=1
    g326: Circle CenterX=1.57905 CenterY=-89.8542 CenterZ=0 NormalX=0 NormalY=0 NormalZ=1 AngleXU=0 Radius=1
    g327: BSplineCurve PolesCount=3 KnotsCount=2 Degree=2 IsPeriodic=0
    g328: GeomPoint X=2.07281 Y=-91.7794 Z=0
    g329: GeomPoint X=1.57905 Y=-89.8542 Z=0
    g330: LineSegment StartX=2.07281 StartY=-91.7794 StartZ=0 EndX=42.0728 EndY=-91.7794 EndZ=0
    g331: LineSegment StartX=46.0728 StartY=-87.7794 StartZ=0 EndX=46.0728 EndY=-69.424 EndZ=0
    g332: LineSegment StartX=42.5666 StartY=-67.3492 StartZ=0 EndX=1.57905 EndY=-89.8542 EndZ=0
    g333: Circle CenterX=322.073 CenterY=76.4095 CenterZ=0 NormalX=0 NormalY=0 NormalZ=1 AngleXU=0 Radius=4
    g334: BSplineCurve PolesCount=3 KnotsCount=2 Degree=2 IsPeriodic=0
    g335: GeomPoint X=318.073 Y=72.4095 Z=0
    g336: GeomPoint X=322.073 Y=76.4095 Z=0
    g337: Circle CenterX=375.073 CenterY=72.4095 CenterZ=0 NormalX=0 NormalY=0 NormalZ=1 AngleXU=0 Radius=1
    g338: Circle CenterX=375.073 CenterY=76.4095 CenterZ=0 NormalX=0 NormalY=0 NormalZ=1 AngleXU=0 Radius=1
    g339: Circle CenterX=371.073 CenterY=76.4095 CenterZ=0 NormalX=0 NormalY=0 NormalZ=1 AngleXU=0 Radius=1
    g340: BSplineCurve PolesCount=3 KnotsCount=2 Degree=2 IsPeriodic=0
    g341: GeomPoint X=375.073 Y=72.4095 Z=0
    g342: GeomPoint X=371.073 Y=76.4095 Z=0
    g343: LineSegment StartX=322.073 StartY=76.4095 StartZ=0 EndX=371.073 EndY=76.4095 EndZ=0
    g344: LineSegment StartX=318.073 StartY=72.4095 StartZ=0 EndX=318.073 EndY=-47.4805 EndZ=0
    g345: LineSegment StartX=375.073 StartY=72.4095 StartZ=0 EndX=375.073 EndY=-78.7896 EndZ=0
    g346: ArcOfCircle CenterX=-26.9272 CenterY=22.1087 CenterZ=0 NormalX=0 NormalY=0 NormalZ=1 AngleXU=0 Radius=4 StartAngle=5e-16 EndAngle=3.14159
    g347: LineSegment StartX=-30.9272 StartY=22.1087 StartZ=0 EndX=-34.9272 EndY=-83.7794 EndZ=0
    g348: LineSegment StartX=-18.9272 StartY=-83.7794 StartZ=0 EndX=-22.9272 EndY=22.1087 EndZ=0
  constraints (572):
    c: Coincident(g0,g2)
    c: Block(g0)
    c: Block(g1)
    c: Vertical(g3)
    c: Vertical(g4)
    c: Block(g4)
    c: Block(g3)
    c: Tangent(g6,g7) = 1.5708
    c: Tangent(g7,g9) = 1.5708
    c: Equal(g6,g9)
    c: Coincident(g8,g6)
    c: Coincident(g8,g9)
    c: Block(g7)
    c: Block(g8)
    c: Weight(g10) = 1
    c: Equal(g10,g11)
    c: Equal(g10,g12)
    c: InternalAlignment(g10,g13)
    c: InternalAlignment(g11,g13)
    c: InternalAlignment(g12,g13)
    c: InternalAlignment(g14,g13)
    c: InternalAlignment(g15,g13)
    c: Weight(g16) = 1
    c: Equal(g16,g17)
    c: Equal(g16,g18)
    c: InternalAlignment(g16,g19)
    c: InternalAlignment(g17,g19)
    c: InternalAlignment(g18,g19)
    c: InternalAlignment(g20,g19)
    c: InternalAlignment(g21,g19)
    c: Block(g19)
    c: Block(g13)
    c: Weight(g22) = 1
    c: Equal(g22,g23)
    c: Equal(g22,g24)
    c: InternalAlignment(g22,g25)
    c: InternalAlignment(g23,g25)
    c: InternalAlignment(g24,g25)
    c: InternalAlignment(g26,g25)
    c: InternalAlignment(g27,g25)
    c: Weight(g28) = 1
    c: Equal(g28,g29)
    c: Equal(g28,g30)
    c: InternalAlignment(g28,g31)
    c: InternalAlignment(g29,g31)
    c: InternalAlignment(g30,g31)
    c: InternalAlignment(g32,g31)
    c: InternalAlignment(g33,g31)
    c: Block(g31)
    c: Block(g25)
    c: Weight(g34) = 1
    c: Equal(g34,g35)
    c: Equal(g34,g36)
    c: InternalAlignment(g34,g37)
    c: InternalAlignment(g35,g37)
    c: InternalAlignment(g36,g37)
    c: InternalAlignment(g38,g37)
    c: InternalAlignment(g39,g37)
    c: Weight(g40) = 1
    c: Equal(g40,g41)
    c: Equal(g40,g42)
    c: InternalAlignment(g40,g43)
    c: InternalAlignment(g41,g43)
    c: InternalAlignment(g42,g43)
    c: InternalAlignment(g44,g43)
    c: InternalAlignment(g45,g43)
    c: Block(g37)
    c: Block(g43)
    c: Coincident(g46,g4)
    c: Coincident(g46,g3)
    c: Horizontal(g46)
    c: Distance(g46) = 450
    c: Coincident(g47,g4)
    c: Coincident(g47,g3)
    c: Horizontal(g47)
    c: Horizontal(g48)
    c: Coincident(g2,g48)
    c: Block(g48)
    c: Coincident(g1,g48)
    c: Weight(g49) = 1
    c: Equal(g49,g50)
    c: Equal(g49,g51)
    c: InternalAlignment(g49,g52)
    c: InternalAlignment(g50,g52)
    c: InternalAlignment(g51,g52)
    c: InternalAlignment(g53,g52)
    c: InternalAlignment(g54,g52)
    c: Block(g52)
    c: Weight(g55) = 1
    c: Equal(g55,g56)
    c: Equal(g55,g57)
    c: InternalAlignment(g55,g58)
    c: InternalAlignment(g56,g58)
    c: InternalAlignment(g57,g58)
    c: InternalAlignment(g59,g58)
    c: InternalAlignment(g60,g58)
    c: Block(g58)
    c: Weight(g61) = 1
    c: Equal(g61,g62)
    c: Equal(g61,g63)
    c: InternalAlignment(g61,g64)
    c: InternalAlignment(g62,g64)
    c: InternalAlignment(g63,g64)
    c: InternalAlignment(g65,g64)
    c: InternalAlignment(g66,g64)
    c: Block(g64)
    c: Weight(g67) = 1
    c: Equal(g67,g68)
    c: Equal(g67,g69)
    c: InternalAlignment(g67,g70)
    c: InternalAlignment(g68,g70)
    c: InternalAlignment(g69,g70)
    c: InternalAlignment(g71,g70)
    c: InternalAlignment(g72,g70)
    c: Block(g70)
    c: Weight(g73) = 1
    c: Equal(g73,g74)
    c: Equal(g73,g75)
    c: InternalAlignment(g73,g76)
    c: InternalAlignment(g74,g76)
    c: InternalAlignment(g75,g76)
    c: InternalAlignment(g77,g76)
    c: InternalAlignment(g78,g76)
    c: Weight(g79) = 1
    c: Equal(g79,g80)
    c: Equal(g79,g81)
    c: InternalAlignment(g79,g82)
    c: InternalAlignment(g80,g82)
    c: InternalAlignment(g81,g82)
    c: InternalAlignment(g83,g82)
    c: InternalAlignment(g84,g82)
    c: Block(g76)
    c: Block(g82)
    c: Coincident(g85,g76)
    c: Coincident(g85,g82)
    c: Vertical(g85)
    c: Coincident(g86,g76)
    c: Coincident(g86,g58)
    c: Coincident(g87,g58)
    c: Coincident(g87,g82)
    c: Weight(g88) = 1
    c: Equal(g88,g89)
    c: Equal(g88,g90)
    c: InternalAlignment(g88,g91)
    c: InternalAlignment(g89,g91)
    c: InternalAlignment(g90,g91)
    c: InternalAlignment(g92,g91)
    c: InternalAlignment(g93,g91)
    c: Weight(g94) = 1
    c: Equal(g94,g95)
    c: Equal(g94,g96)
    c: InternalAlignment(g94,g97)
    c: InternalAlignment(g95,g97)
    c: InternalAlignment(g96,g97)
    c: InternalAlignment(g98,g97)
    c: InternalAlignment(g99,g97)
    c: Block(g91)
    c: Block(g97)
    c: Coincident(g100,g91)
    c: Coincident(g100,g97)
    c: Vertical(g100)
    c: Coincident(g101,g91)
    c: Coincident(g101,g52)
    c: Coincident(g102,g52)
    c: Coincident(g102,g97)
    c: Weight(g103) = 1
    c: Equal(g103,g104)
    c: Equal(g103,g105)
    c: InternalAlignment(g103,g106)
    c: InternalAlignment(g104,g106)
    c: InternalAlignment(g105,g106)
    c: InternalAlignment(g107,g106)
    c: InternalAlignment(g108,g106)
    c: Weight(g109) = 1
    c: Equal(g109,g110)
    c: Equal(g109,g111)
    c: InternalAlignment(g109,g112)
    c: InternalAlignment(g110,g112)
    c: InternalAlignment(g111,g112)
    c: InternalAlignment(g113,g112)
    c: InternalAlignment(g114,g112)
    c: Block(g106)
    c: Block(g112)
    c: Coincident(g115,g106)
    c: Coincident(g115,g112)
    c: Vertical(g115)
    c: Coincident(g116,g112)
    c: Coincident(g116,g70)
    c: Coincident(g117,g70)
    c: Coincident(g117,g106)
    c: Weight(g118) = 1
    c: Equal(g118,g119)
    c: Equal(g118,g120)
    c: InternalAlignment(g118,g121)
    c: InternalAlignment(g119,g121)
    c: InternalAlignment(g120,g121)
    c: InternalAlignment(g122,g121)
    c: InternalAlignment(g123,g121)
    c: Weight(g124) = 1
    c: Equal(g124,g125)
    c: Equal(g124,g126)
    c: InternalAlignment(g124,g127)
    c: InternalAlignment(g125,g127)
    c: InternalAlignment(g126,g127)
    c: InternalAlignment(g128,g127)
    c: InternalAlignment(g129,g127)
    c: Block(g121)
    c: Block(g127)
    c: Coincident(g130,g121)
    c: Coincident(g130,g127)
    c: Vertical(g130)
    c: Coincident(g131,g127)
    c: Coincident(g131,g64)
    c: Coincident(g132,g64)
    c: Coincident(g132,g121)
    c: Weight(g133) = 1
    c: Equal(g133,g134)
    c: Equal(g133,g135)
    c: InternalAlignment(g133,g136)
    c: InternalAlignment(g134,g136)
    c: InternalAlignment(g135,g136)
    c: InternalAlignment(g137,g136)
    c: InternalAlignment(g138,g136)
    c: Weight(g139) = 1
    c: Equal(g139,g140)
    c: Equal(g139,g141)
    c: InternalAlignment(g139,g142)
    c: InternalAlignment(g140,g142)
    c: InternalAlignment(g141,g142)
    c: InternalAlignment(g143,g142)
    c: InternalAlignment(g144,g142)
    c: Weight(g145) = 1
    c: Equal(g145,g146)
    c: Equal(g145,g147)
    c: InternalAlignment(g145,g148)
    c: InternalAlignment(g146,g148)
    c: InternalAlignment(g147,g148)
    c: InternalAlignment(g149,g148)
    c: InternalAlignment(g150,g148)
    c: Weight(g151) = 1
    c: Equal(g151,g152)
    c: Equal(g151,g153)
    c: InternalAlignment(g151,g154)
    c: InternalAlignment(g152,g154)
    c: InternalAlignment(g153,g154)
    c: InternalAlignment(g155,g154)
    c: InternalAlignment(g156,g154)
    c: Block(g154)
    c: Block(g148)
    c: Block(g142)
    c: Block(g136)
    c: Coincident(g157,g31)
    c: Coincident(g157,g154)
    c: Coincident(g158,g154)
    c: Coincident(g158,g148)
    c: Horizontal(g158)
    c: Coincident(g159,g148)
    c: Coincident(g159,g31)
    c: Vertical(g159)
    c: Coincident(g160,g25)
    c: Coincident(g160,g142)
    c: Vertical(g160)
    c: Coincident(g161,g142)
    c: Coincident(g161,g136)
    c: Horizontal(g161)
    c: Coincident(g162,g136)
    c: Coincident(g162,g25)
    c: Weight(g163) = 1
    c: Equal(g163,g164)
    c: Equal(g163,g165)
    c: InternalAlignment(g163,g166)
    c: InternalAlignment(g164,g166)
    c: InternalAlignment(g165,g166)
    c: InternalAlignment(g167,g166)
    c: InternalAlignment(g168,g166)
    c: Weight(g169) = 1
    c: Equal(g169,g170)
    c: Equal(g169,g171)
    c: InternalAlignment(g169,g172)
    c: InternalAlignment(g170,g172)
    c: InternalAlignment(g171,g172)
    c: InternalAlignment(g173,g172)
    c: InternalAlignment(g174,g172)
    c: Weight(g175) = 1
    c: Equal(g175,g176)
    c: Equal(g175,g177)
    c: InternalAlignment(g175,g178)
    c: InternalAlignment(g176,g178)
    c: InternalAlignment(g177,g178)
    c: InternalAlignment(g179,g178)
    c: InternalAlignment(g180,g178)
    c: Weight(g181) = 1
    c: Equal(g181,g182)
    c: Equal(g181,g183)
    c: InternalAlignment(g181,g184)
    c: InternalAlignment(g182,g184)
    c: InternalAlignment(g183,g184)
    c: InternalAlignment(g185,g184)
    c: InternalAlignment(g186,g184)
    c: Block(g184)
    c: Block(g178)
    c: Block(g172)
    c: Block(g166)
    c: Coincident(g187,g184)
    c: Coincident(g187,g178)
    c: Horizontal(g187)
    c: Coincident(g188,g178)
    c: Coincident(g188,g13)
    c: Vertical(g188)
    c: Coincident(g189,g19)
    c: Coincident(g189,g172)
    c: Vertical(g189)
    c: Coincident(g190,g172)
    c: Coincident(g190,g166)
    c: Horizontal(g190)
    c: Coincident(g191,g166)
    c: Coincident(g191,g19)
    c: Coincident(g192,g13)
    c: Weight(g193) = 1
    c: Equal(g193,g194)
    c: Equal(g193,g195)
    c: InternalAlignment(g193,g196)
    c: InternalAlignment(g194,g196)
    c: InternalAlignment(g195,g196)
    c: InternalAlignment(g197,g196)
    c: InternalAlignment(g198,g196)
    c: Weight(g199) = 1
    c: Equal(g199,g200)
    c: Equal(g199,g201)
    c: InternalAlignment(g199,g202)
    c: InternalAlignment(g200,g202)
    c: InternalAlignment(g201,g202)
    c: InternalAlignment(g203,g202)
    c: InternalAlignment(g204,g202)
    c: Block(g202)
    c: Block(g196)
    c: Coincident(g205,g202)
    c: Coincident(g205,g37)
    c: Coincident(g206,g37)
    c: Coincident(g206,g196)
    c: Coincident(g207,g196)
    c: Coincident(g207,g202)
    c: Vertical(g207)
    c: Weight(g208) = 1
    c: Equal(g208,g209)
    c: Equal(g208,g210)
    c: InternalAlignment(g208,g211)
    c: InternalAlignment(g209,g211)
    c: InternalAlignment(g210,g211)
    c: InternalAlignment(g212,g211)
    c: InternalAlignment(g213,g211)
    c: Weight(g214) = 1
    c: Equal(g214,g215)
    c: Equal(g214,g216)
    c: InternalAlignment(g214,g217)
    c: InternalAlignment(g215,g217)
    c: InternalAlignment(g216,g217)
    c: InternalAlignment(g218,g217)
    c: InternalAlignment(g219,g217)
    c: Block(g217)
    c: Block(g211)
    c: Coincident(g220,g211)
    c: Coincident(g220,g43)
    c: Coincident(g221,g43)
    c: Coincident(g221,g217)
    c: Coincident(g222,g217)
    c: Coincident(g222,g211)
    c: Vertical(g222)
    c: Horizontal(g223)
    c: Block(g223)
    c: Vertical(g224)
    c: Block(g224)
    c: Block(g225)
    c: Weight(g226) = 1
    c: Equal(g226,g227)
    c: Equal(g226,g228)
    c: InternalAlignment(g226,g229)
    c: InternalAlignment(g227,g229)
    c: InternalAlignment(g228,g229)
    c: InternalAlignment(g230,g229)
    c: InternalAlignment(g231,g229)
    c: Weight(g232) = 1
    c: Equal(g232,g233)
    c: Equal(g232,g234)
    c: InternalAlignment(g232,g235)
    c: InternalAlignment(g233,g235)
    c: InternalAlignment(g234,g235)
    c: InternalAlignment(g236,g235)
    c: InternalAlignment(g237,g235)
    c: Weight(g238) = 1
    c: Equal(g238,g239)
    c: Equal(g238,g240)
    c: InternalAlignment(g238,g241)
    c: InternalAlignment(g239,g241)
    c: InternalAlignment(g240,g241)
    c: InternalAlignment(g242,g241)
    c: InternalAlignment(g243,g241)
    c: Weight(g244) = 1
    c: Equal(g244,g245)
    c: Equal(g244,g246)
    c: InternalAlignment(g244,g247)
    c: InternalAlignment(g245,g247)
    c: InternalAlignment(g246,g247)
    c: InternalAlignment(g248,g247)
    c: InternalAlignment(g249,g247)
    c: Block(g229)
    c: Block(g235)
    c: Block(g241)
    c: Block(g247)
    c: Coincident(g250,g235)
    c: Coincident(g250,g229)
    c: Horizontal(g250)
    c: Block(g192)
    c: Weight(g251) = 1
    c: Equal(g251,g252)
    c: Equal(g251,g253)
    c: InternalAlignment(g251,g254)
    c: InternalAlignment(g252,g254)
    c: InternalAlignment(g253,g254)
    c: InternalAlignment(g255,g254)
    c: InternalAlignment(g256,g254)
    c: Weight(g257) = 1
    c: Equal(g257,g258)
    c: Equal(g257,g259)
    c: InternalAlignment(g257,g260)
    c: InternalAlignment(g258,g260)
    c: InternalAlignment(g259,g260)
    c: InternalAlignment(g261,g260)
    c: InternalAlignment(g262,g260)
    c: Block(g254)
    c: Block(g260)
    c: Coincident(g263,g254)
    c: Coincident(g263,g260)
    c: Weight(g264) = 1
    c: Equal(g264,g265)
    c: Equal(g264,g266)
    c: InternalAlignment(g264,g267)
    c: InternalAlignment(g265,g267)
    c: InternalAlignment(g266,g267)
    c: InternalAlignment(g268,g267)
    c: InternalAlignment(g269,g267)
    c: Weight(g270) = 1
    c: Equal(g270,g271)
    c: Equal(g270,g272)
    c: InternalAlignment(g270,g273)
    c: InternalAlignment(g271,g273)
    c: InternalAlignment(g272,g273)
    c: InternalAlignment(g274,g273)
    c: InternalAlignment(g275,g273)
    c: Weight(g276) = 1
    c: Equal(g276,g277)
    c: Equal(g276,g278)
    c: InternalAlignment(g276,g279)
    c: InternalAlignment(g277,g279)
    c: InternalAlignment(g278,g279)
    c: InternalAlignment(g280,g279)
    c: InternalAlignment(g281,g279)
    c: Block(g279)
    c: Block(g273)
    c: Block(g267)
    c: Coincident(g282,g273)
    c: Coincident(g282,g267)
    c: Coincident(g283,g267)
    c: Coincident(g283,g279)
    c: Vertical(g283)
    c: Coincident(g284,g279)
    c: Coincident(g284,g273)
    c: Horizontal(g284)
    c: Weight(g285) = 1
    c: Equal(g285,g286)
    c: InternalAlignment(g285,g287)
    c: InternalAlignment(g286,g287)
    c: InternalAlignment(g288,g287)
    c: InternalAlignment(g289,g287)
    c: Weight(g290) = 1
    c: InternalAlignment(g291,g293)
    c: InternalAlignment(g292,g293)
    c: InternalAlignment(g294,g293)
    c: InternalAlignment(g295,g293)
    c: Weight(g296) = 1
    c: Equal(g296,g297)
    c: Equal(g296,g298)
    c: InternalAlignment(g296,g299)
    c: InternalAlignment(g297,g299)
    c: InternalAlignment(g298,g299)
    c: InternalAlignment(g300,g299)
    c: InternalAlignment(g301,g299)
    c: Equal(g302,g303)
    c: Equal(g302,g304)
    c: InternalAlignment(g302,g305)
    c: InternalAlignment(g303,g305)
    c: InternalAlignment(g304,g305)
    c: InternalAlignment(g306,g305)
    c: InternalAlignment(g307,g305)
    c: Block(g293)
    c: Block(g299)
    c: Block(g305)
    c: Block(g287)
    c: Coincident(g308,g287)
    c: Coincident(g308,g293)
    c: Horizontal(g308)
    c: Coincident(g309,g293)
    c: Coincident(g309,g299)
    c: Vertical(g309)
    c: Coincident(g310,g299)
    c: Coincident(g310,g305)
    c: Horizontal(g310)
    c: Coincident(g311,g305)
    c: Coincident(g311,g287)
    c: Weight(g312) = 1
    c: Equal(g312,g313)
    c: Equal(g312,g314)
    c: InternalAlignment(g312,g315)
    c: InternalAlignment(g313,g315)
    c: InternalAlignment(g314,g315)
    c: InternalAlignment(g316,g315)
    c: InternalAlignment(g317,g315)
    c: Weight(g318) = 1
    c: Equal(g318,g319)
    c: Equal(g318,g320)
    c: InternalAlignment(g318,g321)
    c: InternalAlignment(g319,g321)
    c: InternalAlignment(g320,g321)
    c: InternalAlignment(g322,g321)
    c: InternalAlignment(g323,g321)
    c: Weight(g324) = 1
    c: Equal(g324,g325)
    c: Equal(g324,g326)
    c: InternalAlignment(g324,g327)
    c: InternalAlignment(g325,g327)
    c: InternalAlignment(g326,g327)
    c: InternalAlignment(g328,g327)
    c: InternalAlignment(g329,g327)
    c: Block(g327)
    c: Block(g321)
    c: Block(g315)
    c: Coincident(g330,g327)
    c: Coincident(g330,g321)
    c: Horizontal(g330)
    c: Coincident(g331,g321)
    c: Coincident(g331,g315)
    c: Vertical(g331)
    c: Coincident(g332,g315)
    c: Coincident(g332,g327)
    c: InternalAlignment(g333,g334)
    c: InternalAlignment(g335,g334)
    c: InternalAlignment(g336,g334)
    c: Block(g334)
    c: Equal(g337,g338)
    c: Equal(g337,g339)
    c: InternalAlignment(g337,g340)
    c: InternalAlignment(g338,g340)
    c: InternalAlignment(g339,g340)
    c: InternalAlignment(g341,g340)
    c: InternalAlignment(g342,g340)
    c: Block(g340)
    c: Coincident(g343,g334)
    c: Horizontal(g343)
    c: Block(g343)
    c: Coincident(g344,g334)
    c: Coincident(g344,g260)
    c: Vertical(g344)
    c: Coincident(g345,g340)
    c: Coincident(g345,g254)
    c: Vertical(g345)
    c: Coincident(g347,g5)
    c: Coincident(g348,g5)
    c: Block(g346)
    c: Block(g5)
    c: Block(g348)
    c: Block(g347)
    c: Distance(g344) = 119.89
FEATURE [Sketcher::SketchObject] Sketch001
  FullyConstrained = true
  MapMode = 4
  Placement = pos=(0,0,0) rot=(0.57735,0.57735,0.57735;2.0944rad)
  Support = -> [Sketch]
  sketch-geometry (46):
    g0: BSplineCurve PolesCount=3 KnotsCount=2 Degree=2 IsPeriodic=0
    g1: ArcOfCircle CenterX=73.1223 CenterY=-32.291 CenterZ=0 NormalX=0 NormalY=0 NormalZ=1 AngleXU=0 Radius=13 StartAngle=5.92268 EndAngle=9.06428
    g2: ArcOfCircle CenterX=66.7816 CenterY=-49.1439 CenterZ=0 NormalX=0 NormalY=0 NormalZ=1 AngleXU=0 Radius=13 StartAngle=2.78068 EndAngle=5.92131
    g3: ArcOfCircle CenterX=55.9263 CenterY=-78.1807 CenterZ=0 NormalX=0 NormalY=0 NormalZ=1 AngleXU=0 Radius=13 StartAngle=5.92268 EndAngle=9.06428
    g4: ArcOfCircle CenterX=49.5884 CenterY=-95.0342 CenterZ=0 NormalX=0 NormalY=0 NormalZ=1 AngleXU=0 Radius=13 StartAngle=2.78068 EndAngle=5.92131
    g5: ArcOfCircle CenterX=38.7206 CenterY=-124.067 CenterZ=0 NormalX=0 NormalY=0 NormalZ=1 AngleXU=0 Radius=13 StartAngle=5.92268 EndAngle=9.06428
    g6: ArcOfCircle CenterX=32.3875 CenterY=-140.92 CenterZ=0 NormalX=0 NormalY=0 NormalZ=1 AngleXU=0 Radius=13 StartAngle=2.78068 EndAngle=5.92131
    g7: ArcOfCircle CenterX=21.4715 CenterY=-169.934 CenterZ=0 NormalX=0 NormalY=0 NormalZ=1 AngleXU=0 Radius=13 StartAngle=5.92268 EndAngle=9.06428
    g8: ArcOfCircle CenterX=15.1336 CenterY=-186.787 CenterZ=0 NormalX=0 NormalY=0 NormalZ=1 AngleXU=0 Radius=13 StartAngle=2.78068 EndAngle=5.92131
    g9-g12: Circle x4 (B-spline internal-alignment scaffolding for g13; pole/knot coordinates omitted)
    g13: BSplineCurve PolesCount=4 KnotsCount=2 Degree=3 IsPeriodic=0
    g14: GeomPoint X=28.8094 Y=-19.0875 Z=0
    g15: GeomPoint X=47.0443 Y=-50.4712 Z=0
    g16: Circle CenterX=53.5586 CenterY=-23.2695 CenterZ=0 NormalX=0 NormalY=0 NormalZ=1 AngleXU=0 Radius=3.24518
    g17: Circle CenterX=-195.441 CenterY=-127.082 CenterZ=0 NormalX=0 NormalY=0 NormalZ=1 AngleXU=0 Radius=1
    g18: Circle CenterX=-8.24091 CenterY=-197.481 CenterZ=0 NormalX=0 NormalY=0 NormalZ=1 AngleXU=0 Radius=1
    g19: Circle CenterX=12.8789 CenterY=-141.321 CenterZ=0 NormalX=0 NormalY=0 NormalZ=1 AngleXU=0 Radius=1
    g20: BSplineCurve PolesCount=3 KnotsCount=2 Degree=2 IsPeriodic=0
    g21: GeomPoint X=-195.441 Y=-127.082 Z=0
    g22: GeomPoint X=12.8789 Y=-141.321 Z=0
    g23: Circle CenterX=-12.8016 CenterY=-179.036 CenterZ=0 NormalX=0 NormalY=0 NormalZ=1 AngleXU=0 Radius=10.5072
    g24: Circle CenterX=0.933922 CenterY=-166.43 CenterZ=0 NormalX=0 NormalY=0 NormalZ=1 AngleXU=0 Radius=3.26661
    g25: Circle CenterX=-33.5518 CenterY=-176.44 CenterZ=0 NormalX=0 NormalY=0 NormalZ=1 AngleXU=0 Radius=5.64388
    g26: Circle CenterX=-47.2366 CenterY=-173.859 CenterZ=0 NormalX=0 NormalY=0 NormalZ=1 AngleXU=0 Radius=3.01653
    g27: Circle CenterX=-56.2595 CenterY=-171.456 CenterZ=0 NormalX=0 NormalY=0 NormalZ=1 AngleXU=0 Radius=2.12826
    g28: ArcOfCircle CenterX=51.2151 CenterY=-198.473 CenterZ=0 NormalX=0 NormalY=0 NormalZ=1 AngleXU=0 Radius=20 StartAngle=2.78189 EndAngle=4.35269
    g29: LineSegment StartX=32.4951 StartY=-191.433 StartZ=0 EndX=94.6578 EndY=-26.1352 EndZ=0
    g30: LineSegment StartX=43.1192 StartY=-220.001 StartZ=0 EndX=-196.497 EndY=-129.89 EndZ=0
    g31: LineSegment StartX=43.1192 StartY=-220.001 StartZ=0 EndX=44.1752 EndY=-217.193 EndZ=0
    g32: LineSegment StartX=117.223 StartY=-19.0875 StartZ=0 EndX=117.223 EndY=-16.0875 EndZ=0
    g33: LineSegment StartX=117.223 StartY=-16.0875 StartZ=0 EndX=17.2232 EndY=-16.0875 EndZ=0
    g34: LineSegment StartX=17.2232 StartY=-16.0875 StartZ=0 EndX=17.2232 EndY=-19.0875 EndZ=0
    g35: LineSegment StartX=28.8094 StartY=-19.0875 StartZ=0 EndX=17.2232 EndY=-19.0875 EndZ=0
    g36: LineSegment StartX=47.0443 StartY=-50.4712 StartZ=0 EndX=12.8789 EndY=-141.321 EndZ=0
    g37: LineSegment StartX=-195.441 StartY=-127.082 StartZ=0 EndX=-196.497 EndY=-129.89 EndZ=0
    g38: LineSegment StartX=85.2866 StartY=-36.8766 StartZ=0 EndX=78.9396 EndY=-53.7463 EndZ=0
    g39: LineSegment StartX=60.9579 StartY=-27.7053 StartZ=0 EndX=54.6191 EndY=-44.5532 EndZ=0
    g40: LineSegment StartX=68.0907 StartY=-82.7664 StartZ=0 EndX=61.7465 EndY=-99.6365 EndZ=0
    g41: LineSegment StartX=43.7619 StartY=-73.595 StartZ=0 EndX=37.426 EndY=-90.4435 EndZ=0
    g42: LineSegment StartX=50.885 StartY=-128.652 StartZ=0 EndX=44.5456 EndY=-145.522 EndZ=0
    g43: LineSegment StartX=26.5562 StartY=-119.481 StartZ=0 EndX=20.2251 EndY=-136.329 EndZ=0
    g44: LineSegment StartX=9.3071 StartY=-165.349 StartZ=0 EndX=2.97115 EndY=-182.197 EndZ=0
    g45: LineSegment StartX=33.6358 StartY=-174.52 StartZ=0 EndX=27.2917 EndY=-191.39 EndZ=0
  constraints (71):
    c: Block(g0)
    c: Block(g1)
    c: Block(g2)
    c: Block(g4)
    c: Block(g3)
    c: Block(g6)
    c: Block(g5)
    c: Block(g8)
    c: Block(g7)
    c: Weight(g9) = 1
    c: Equal(g9,g10)
    c: Equal(g9,g11)
    c: Equal(g9,g12)
    c: InternalAlignment(g9-g12 -> g13) x4
    c: InternalAlignment(g14,g13)
    c: InternalAlignment(g15,g13)
    c: Block(g16)
    c: Weight(g17) = 1
    c: Equal(g17,g18)
    c: Equal(g17,g19)
    c: InternalAlignment(g17,g20)
    c: InternalAlignment(g18,g20)
    c: InternalAlignment(g19,g20)
    c: InternalAlignment(g21,g20)
    c: InternalAlignment(g22,g20)
    c: Block(g20)
    c: Block(g23)
    c: Block(g24)
    c: Block(g25)
    c: Block(g26)
    c: Block(g27)
    c: Block(g28)
    c: Coincident(g29,g28)
    c: Coincident(g29,g0)
    c: Block(g13)
    c: Coincident(g31,g30)
    c: Coincident(g31,g28)
    c: Block(g31)
    c: Coincident(g32,g0)
    c: Vertical(g32)
    c: Coincident(g33,g32)
    c: Horizontal(g33)
    c: Coincident(g34,g33)
    c: Vertical(g34)
    c: Block(g33)
    c: Coincident(g35,g13)
    c: Coincident(g35,g34)
    c: Horizontal(g35)
    c: Coincident(g36,g13)
    c: Coincident(g36,g20)
    c: Coincident(g37,g20)
    c: Coincident(g37,g30)
    c: Block(g30)
    c: Coincident(g38,g1)
    c: Coincident(g38,g2)
    c: Coincident(g39,g1)
    c: Coincident(g39,g2)
    c: Coincident(g40,g3)
    c: Coincident(g40,g4)
    c: Coincident(g41,g3)
    c: Coincident(g41,g4)
    c: Coincident(g42,g5)
    c: Coincident(g42,g6)
    c: Coincident(g43,g5)
    c: Coincident(g43,g6)
    c: Coincident(g44,g7)
    c: Coincident(g44,g8)
    c: Coincident(g45,g7)
    c: Coincident(g45,g8)
    c: Distance(g30) = 256
    c: Distance(g33) = 100
FEATURE [Part::Extrusion] Extrude002
  Base = -> Sketch001
  Dir = (1,0,0)
  DirMode = 2
  FaceMakerClass = Part::FaceMakerBullseye
  LengthFwd = 8
  LengthRev = 0
  Solid = true
  Symmetric = false
FEATURE [Sketcher::SketchObject] Sketch002
  FullyConstrained = true
  sketch-geometry (20):
    g0: LineSegment StartX=-2.77179 StartY=-200.304 StartZ=0 EndX=5.22821 EndY=-200.304 EndZ=0
    g1: LineSegment StartX=5.22821 StartY=-200.304 StartZ=0 EndX=5.22821 EndY=-197.304 EndZ=0
    g2: LineSegment StartX=-2.77179 StartY=-200.304 StartZ=0 EndX=-2.77179 EndY=-197.304 EndZ=0
    g3: LineSegment StartX=5.22821 StartY=-197.304 StartZ=0 EndX=8.22821 EndY=-197.304 EndZ=0
    g4: LineSegment StartX=-2.77179 StartY=-197.304 StartZ=0 EndX=-5.77179 EndY=-197.304 EndZ=0
    g5: LineSegment StartX=19.2282 StartY=-203.304 StartZ=0 EndX=19.2282 EndY=-206.304 EndZ=0
    g6: LineSegment StartX=-16.7718 StartY=-203.304 StartZ=0 EndX=-16.7718 EndY=-206.304 EndZ=0
    g7: LineSegment StartX=-16.7718 StartY=-206.304 StartZ=0 EndX=19.2282 EndY=-206.304 EndZ=0
    g8: Circle CenterX=-16.7718 CenterY=-203.304 CenterZ=0 NormalX=0 NormalY=0 NormalZ=1 AngleXU=0 Radius=1
    g9: Circle CenterX=-5.77179 CenterY=-203.304 CenterZ=0 NormalX=0 NormalY=0 NormalZ=1 AngleXU=0 Radius=1
    g10: Circle CenterX=-5.77179 CenterY=-197.304 CenterZ=0 NormalX=0 NormalY=0 NormalZ=1 AngleXU=0 Radius=1
    g11: BSplineCurve PolesCount=3 KnotsCount=2 Degree=2 IsPeriodic=0
    g12: GeomPoint X=-16.7718 Y=-203.304 Z=0
    g13: GeomPoint X=-5.77179 Y=-197.304 Z=0
    g14: Circle CenterX=19.2282 CenterY=-203.304 CenterZ=0 NormalX=0 NormalY=0 NormalZ=1 AngleXU=0 Radius=1
    g15: Circle CenterX=8.22821 CenterY=-203.304 CenterZ=0 NormalX=0 NormalY=0 NormalZ=1 AngleXU=0 Radius=1
    g16: Circle CenterX=8.22821 CenterY=-197.304 CenterZ=0 NormalX=0 NormalY=0 NormalZ=1 AngleXU=0 Radius=1
    g17: BSplineCurve PolesCount=3 KnotsCount=2 Degree=2 IsPeriodic=0
    g18: GeomPoint X=19.2282 Y=-203.304 Z=0
    g19: GeomPoint X=8.22821 Y=-197.304 Z=0
  constraints (41):
    c: Horizontal(g0)
    c: Distance(g0) = 8
    c: Coincident(g1,g0)
    c: Vertical(g1)
    c: Distance(g1) = 3
    c: Coincident(g2,g0)
    c: Vertical(g2)
    c: Distance(g2) = 3
    c: Coincident(g3,g1)
    c: Horizontal(g3)
    c: Distance(g3) = 3
    c: Coincident(g4,g2)
    c: Horizontal(g4)
    c: Distance(g4) = 3
    c: Vertical(g5)
    c: Vertical(g6)
    c: Coincident(g7,g6)
    c: Coincident(g7,g5)
    c: Weight(g8) = 1
    c: Equal(g8,g9)
    c: Equal(g8,g10)
    c: Coincident(g11,g4)
    c: InternalAlignment(g8,g11)
    c: InternalAlignment(g9,g11)
    c: InternalAlignment(g10,g11)
    c: InternalAlignment(g12,g11)
    c: InternalAlignment(g13,g11)
    c: Coincident(g17,g5)
    c: Weight(g14) = 1
    c: Equal(g14,g15)
    c: Equal(g14,g16)
    c: Coincident(g17,g3)
    c: InternalAlignment(g14,g17)
    c: InternalAlignment(g15,g17)
    c: InternalAlignment(g16,g17)
    c: InternalAlignment(g18,g17)
    c: InternalAlignment(g19,g17)
    c: Block(g7)
    c: Block(g17)
    c: Block(g11)
    c: Block(g6)
FEATURE [Part::Extrusion] Extrude003
  Base = -> Sketch002
  Dir = (0,0,1)
  DirMode = 2
  FaceMakerClass = Part::FaceMakerBullseye
  LengthFwd = 260
  LengthRev = 0
  Solid = true
  Symmetric = false
FEATURE [Sketcher::SketchObject] Sketch003
  FullyConstrained = false
  sketch-geometry (393):
    g0: LineSegment StartX=-42.9272 StartY=136.221 StartZ=0 EndX=-42.9272 EndY=-103.779 EndZ=0
    g1: LineSegment StartX=407.073 StartY=136.221 StartZ=0 EndX=407.073 EndY=-103.779 EndZ=0
    g2: ArcOfCircle CenterX=-26.9272 CenterY=-83.7794 CenterZ=0 NormalX=0 NormalY=0 NormalZ=1 AngleXU=0 Radius=8 StartAngle=3.14159 EndAngle=6.28319
    g3: ArcOfCircle CenterX=391.073 CenterY=-83.7794 CenterZ=0 NormalX=0 NormalY=0 NormalZ=1 AngleXU=0 Radius=8 StartAngle=3.14159 EndAngle=6.28319
    g4: Circle CenterX=175.022 CenterY=27.0628 CenterZ=0 NormalX=0 NormalY=0 NormalZ=1 AngleXU=0 Radius=1
    g5: Circle CenterX=179.022 CenterY=24.8665 CenterZ=0 NormalX=0 NormalY=0 NormalZ=1 AngleXU=0 Radius=1
    g6: Circle CenterX=179.022 CenterY=27.0628 CenterZ=0 NormalX=0 NormalY=0 NormalZ=1 AngleXU=0 Radius=1
    g7: BSplineCurve PolesCount=3 KnotsCount=2 Degree=2 IsPeriodic=0
    g8: GeomPoint X=175.022 Y=27.0628 Z=0
    g9: GeomPoint X=179.022 Y=27.0628 Z=0
    g10: Circle CenterX=189.124 CenterY=27.0628 CenterZ=0 NormalX=0 NormalY=0 NormalZ=1 AngleXU=0 Radius=1
    g11: Circle CenterX=185.124 CenterY=24.8665 CenterZ=0 NormalX=0 NormalY=0 NormalZ=1 AngleXU=0 Radius=1
    g12: Circle CenterX=185.124 CenterY=27.0628 CenterZ=0 NormalX=0 NormalY=0 NormalZ=1 AngleXU=0 Radius=1
    g13: BSplineCurve PolesCount=3 KnotsCount=2 Degree=2 IsPeriodic=0
    g14: GeomPoint X=189.124 Y=27.0628 Z=0
    g15: GeomPoint X=185.124 Y=27.0628 Z=0
    g16: Circle CenterX=175.022 CenterY=5.37834 CenterZ=0 NormalX=0 NormalY=0 NormalZ=1 AngleXU=0 Radius=1
    g17: Circle CenterX=179.022 CenterY=7.57463 CenterZ=0 NormalX=0 NormalY=0 NormalZ=1 AngleXU=0 Radius=1
    g18: Circle CenterX=179.022 CenterY=5.34704 CenterZ=0 NormalX=0 NormalY=0 NormalZ=1 AngleXU=0 Radius=1
    g19: BSplineCurve PolesCount=3 KnotsCount=2 Degree=2 IsPeriodic=0
    g20: GeomPoint X=175.022 Y=5.37834 Z=0
    g21: GeomPoint X=179.022 Y=5.34704 Z=0
    g22: Circle CenterX=189.124 CenterY=5.37834 CenterZ=0 NormalX=0 NormalY=0 NormalZ=1 AngleXU=0 Radius=1
    g23: Circle CenterX=185.124 CenterY=7.57463 CenterZ=0 NormalX=0 NormalY=0 NormalZ=1 AngleXU=0 Radius=1
    g24: Circle CenterX=185.124 CenterY=5.34704 CenterZ=0 NormalX=0 NormalY=0 NormalZ=1 AngleXU=0 Radius=1
    g25: BSplineCurve PolesCount=3 KnotsCount=2 Degree=2 IsPeriodic=0
    g26: GeomPoint X=189.124 Y=5.37834 Z=0
    g27: GeomPoint X=185.124 Y=5.34704 Z=0
    g28: Circle CenterX=165.871 CenterY=18.1458 CenterZ=0 NormalX=0 NormalY=0 NormalZ=1 AngleXU=0 Radius=1
    g29: Circle CenterX=169.377 CenterY=16.2206 CenterZ=0 NormalX=0 NormalY=0 NormalZ=1 AngleXU=0 Radius=1
    g30: Circle CenterX=165.871 CenterY=14.2954 CenterZ=0 NormalX=0 NormalY=0 NormalZ=1 AngleXU=0 Radius=1
    g31: BSplineCurve PolesCount=3 KnotsCount=2 Degree=2 IsPeriodic=0
    g32: GeomPoint X=165.871 Y=18.1458 Z=0
    g33: GeomPoint X=165.871 Y=14.2954 Z=0
    g34: Circle CenterX=198.275 CenterY=18.1458 CenterZ=0 NormalX=0 NormalY=0 NormalZ=1 AngleXU=0 Radius=1
    g35: Circle CenterX=194.768 CenterY=16.2206 CenterZ=0 NormalX=0 NormalY=0 NormalZ=1 AngleXU=0 Radius=1
    g36: Circle CenterX=198.275 CenterY=14.2954 CenterZ=0 NormalX=0 NormalY=0 NormalZ=1 AngleXU=0 Radius=1
    g37: BSplineCurve PolesCount=3 KnotsCount=2 Degree=2 IsPeriodic=0
    g38: GeomPoint X=198.275 Y=18.1458 Z=0
    g39: GeomPoint X=198.275 Y=14.2954 Z=0
    g40: LineSegment StartX=407.073 StartY=-103.779 StartZ=0 EndX=-42.9272 EndY=-103.779 EndZ=0
    g41: Circle CenterX=125.607 CenterY=54.1951 CenterZ=0 NormalX=0 NormalY=0 NormalZ=1 AngleXU=0 Radius=1
    g42: Circle CenterX=139.632 CenterY=46.4944 CenterZ=0 NormalX=0 NormalY=0 NormalZ=1 AngleXU=0 Radius=1
    g43: Circle CenterX=127.326 CenterY=56.7187 CenterZ=0 NormalX=0 NormalY=0 NormalZ=1 AngleXU=0 Radius=1
    g44: BSplineCurve PolesCount=3 KnotsCount=2 Degree=2 IsPeriodic=0
    g45: GeomPoint X=125.607 Y=54.1951 Z=0
    g46: GeomPoint X=127.326 Y=56.7187 Z=0
    g47: Circle CenterX=236.821 CenterY=56.7187 CenterZ=0 NormalX=0 NormalY=0 NormalZ=1 AngleXU=0 Radius=1
    g48: Circle CenterX=224.513 CenterY=46.4944 CenterZ=0 NormalX=0 NormalY=0 NormalZ=1 AngleXU=0 Radius=1
    g49: Circle CenterX=238.538 CenterY=54.1951 CenterZ=0 NormalX=0 NormalY=0 NormalZ=1 AngleXU=0 Radius=1
    g50: BSplineCurve PolesCount=3 KnotsCount=2 Degree=2 IsPeriodic=0
    g51: GeomPoint X=236.821 Y=56.7187 Z=0
    g52: GeomPoint X=238.538 Y=54.1951 Z=0
    g53: Circle CenterX=238.538 CenterY=-21.7539 CenterZ=0 NormalX=0 NormalY=0 NormalZ=1 AngleXU=0 Radius=1
    g54: Circle CenterX=224.513 CenterY=-14.0532 CenterZ=0 NormalX=0 NormalY=0 NormalZ=1 AngleXU=0 Radius=1
    g55: Circle CenterX=236.821 CenterY=-24.2775 CenterZ=0 NormalX=0 NormalY=0 NormalZ=1 AngleXU=0 Radius=1
    g56: BSplineCurve PolesCount=3 KnotsCount=2 Degree=2 IsPeriodic=0
    g57: GeomPoint X=238.538 Y=-21.7539 Z=0
    g58: GeomPoint X=236.821 Y=-24.2775 Z=0
    g59: Circle CenterX=125.607 CenterY=-21.7539 CenterZ=0 NormalX=0 NormalY=0 NormalZ=1 AngleXU=0 Radius=1
    g60: Circle CenterX=139.632 CenterY=-14.0532 CenterZ=0 NormalX=0 NormalY=0 NormalZ=1 AngleXU=0 Radius=1
    g61: Circle CenterX=127.325 CenterY=-24.2775 CenterZ=0 NormalX=0 NormalY=0 NormalZ=1 AngleXU=0 Radius=1
    g62: BSplineCurve PolesCount=3 KnotsCount=2 Degree=2 IsPeriodic=0
    g63: GeomPoint X=125.607 Y=-21.7539 Z=0
    g64: GeomPoint X=127.325 Y=-24.2775 Z=0
    g65: Circle CenterX=302.996 CenterY=111.695 CenterZ=0 NormalX=0 NormalY=0 NormalZ=1 AngleXU=0 Radius=1
    g66: Circle CenterX=306.073 CenterY=114.251 CenterZ=0 NormalX=0 NormalY=0 NormalZ=1 AngleXU=0 Radius=1
    g67: Circle CenterX=306.073 CenterY=110.251 CenterZ=0 NormalX=0 NormalY=0 NormalZ=1 AngleXU=0 Radius=1
    g68: BSplineCurve PolesCount=3 KnotsCount=2 Degree=2 IsPeriodic=0
    g69: GeomPoint X=302.996 Y=111.695 Z=0
    g70: GeomPoint X=306.073 Y=110.251 Z=0
    g71: Circle CenterX=306.073 CenterY=95.2763 CenterZ=0 NormalX=0 NormalY=0 NormalZ=1 AngleXU=0 Radius=1
    g72: Circle CenterX=306.073 CenterY=91.2763 CenterZ=0 NormalX=0 NormalY=0 NormalZ=1 AngleXU=0 Radius=1
    g73: Circle CenterX=302.567 CenterY=89.3511 CenterZ=0 NormalX=0 NormalY=0 NormalZ=1 AngleXU=0 Radius=1
    g74: BSplineCurve PolesCount=3 KnotsCount=2 Degree=2 IsPeriodic=0
    g75: GeomPoint X=306.073 Y=95.2763 Z=0
    g76: GeomPoint X=302.567 Y=89.3511 Z=0
    g77: LineSegment StartX=306.073 StartY=110.251 StartZ=0 EndX=306.073 EndY=95.2763 EndZ=0
    g78: LineSegment StartX=302.996 StartY=111.695 StartZ=0 EndX=236.821 EndY=56.7187 EndZ=0
    g79: LineSegment StartX=238.538 StartY=54.1951 StartZ=0 EndX=302.567 EndY=89.3511 EndZ=0
    g80: Circle CenterX=61.1496 CenterY=111.695 CenterZ=0 NormalX=0 NormalY=0 NormalZ=1 AngleXU=0 Radius=1
    g81: Circle CenterX=58.0728 CenterY=114.251 CenterZ=0 NormalX=0 NormalY=0 NormalZ=1 AngleXU=0 Radius=1
    g82: Circle CenterX=58.0728 CenterY=110.251 CenterZ=0 NormalX=0 NormalY=0 NormalZ=1 AngleXU=0 Radius=1
    g83: BSplineCurve PolesCount=3 KnotsCount=2 Degree=2 IsPeriodic=0
    g84: GeomPoint X=61.1496 Y=111.695 Z=0
    g85: GeomPoint X=58.0728 Y=110.251 Z=0
    g86: Circle CenterX=61.5791 CenterY=89.3511 CenterZ=0 NormalX=0 NormalY=0 NormalZ=1 AngleXU=0 Radius=1
    g87: Circle CenterX=58.0728 CenterY=91.2763 CenterZ=0 NormalX=0 NormalY=0 NormalZ=1 AngleXU=0 Radius=1
    g88: Circle CenterX=58.0728 CenterY=95.2763 CenterZ=0 NormalX=0 NormalY=0 NormalZ=1 AngleXU=0 Radius=1
    g89: BSplineCurve PolesCount=3 KnotsCount=2 Degree=2 IsPeriodic=0
    g90: GeomPoint X=61.5791 Y=89.3511 Z=0
    g91: GeomPoint X=58.0728 Y=95.2763 Z=0
    g92: LineSegment StartX=58.0728 StartY=110.251 StartZ=0 EndX=58.0728 EndY=95.2763 EndZ=0
    g93: LineSegment StartX=61.1496 StartY=111.695 StartZ=0 EndX=127.326 EndY=56.7187 EndZ=0
    g94: LineSegment StartX=125.607 StartY=54.1951 StartZ=0 EndX=61.5791 EndY=89.3511 EndZ=0
    g95: Circle CenterX=61.5791 CenterY=-56.9099 CenterZ=0 NormalX=0 NormalY=0 NormalZ=1 AngleXU=0 Radius=1
    g96: Circle CenterX=58.0728 CenterY=-58.8351 CenterZ=0 NormalX=0 NormalY=0 NormalZ=1 AngleXU=0 Radius=1
    g97: Circle CenterX=58.0728 CenterY=-62.8351 CenterZ=0 NormalX=0 NormalY=0 NormalZ=1 AngleXU=0 Radius=1
    g98: BSplineCurve PolesCount=3 KnotsCount=2 Degree=2 IsPeriodic=0
    g99: GeomPoint X=61.5791 Y=-56.9099 Z=0
    g100: GeomPoint X=58.0728 Y=-62.8351 Z=0
    g101: Circle CenterX=58.0728 CenterY=-77.8102 CenterZ=0 NormalX=0 NormalY=0 NormalZ=1 AngleXU=0 Radius=1
    g102: Circle CenterX=58.0728 CenterY=-81.8102 CenterZ=0 NormalX=0 NormalY=0 NormalZ=1 AngleXU=0 Radius=1
    g103: Circle CenterX=61.1496 CenterY=-79.2541 CenterZ=0 NormalX=0 NormalY=0 NormalZ=1 AngleXU=0 Radius=1
    g104: BSplineCurve PolesCount=3 KnotsCount=2 Degree=2 IsPeriodic=0
    g105: GeomPoint X=58.0728 Y=-77.8102 Z=0
    g106: GeomPoint X=61.1496 Y=-79.2541 Z=0
    g107: LineSegment StartX=58.0728 StartY=-62.8351 StartZ=0 EndX=58.0728 EndY=-77.8102 EndZ=0
    g108: LineSegment StartX=61.1496 StartY=-79.2541 StartZ=0 EndX=127.325 EndY=-24.2775 EndZ=0
    g109: LineSegment StartX=125.607 StartY=-21.7539 StartZ=0 EndX=61.5791 EndY=-56.9099 EndZ=0
    g110: Circle CenterX=302.567 CenterY=-56.9099 CenterZ=0 NormalX=0 NormalY=0 NormalZ=1 AngleXU=0 Radius=1
    g111: Circle CenterX=306.073 CenterY=-58.8351 CenterZ=0 NormalX=0 NormalY=0 NormalZ=1 AngleXU=0 Radius=1
    g112: Circle CenterX=306.073 CenterY=-62.8351 CenterZ=0 NormalX=0 NormalY=0 NormalZ=1 AngleXU=0 Radius=1
    g113: BSplineCurve PolesCount=3 KnotsCount=2 Degree=2 IsPeriodic=0
    g114: GeomPoint X=302.567 Y=-56.9099 Z=0
    g115: GeomPoint X=306.073 Y=-62.8351 Z=0
    g116: Circle CenterX=302.996 CenterY=-79.2541 CenterZ=0 NormalX=0 NormalY=0 NormalZ=1 AngleXU=0 Radius=1
    g117: Circle CenterX=306.073 CenterY=-81.8102 CenterZ=0 NormalX=0 NormalY=0 NormalZ=1 AngleXU=0 Radius=1
    g118: Circle CenterX=306.073 CenterY=-77.8102 CenterZ=0 NormalX=0 NormalY=0 NormalZ=1 AngleXU=0 Radius=1
    g119: BSplineCurve PolesCount=3 KnotsCount=2 Degree=2 IsPeriodic=0
    g120: GeomPoint X=302.996 Y=-79.2541 Z=0
    g121: GeomPoint X=306.073 Y=-77.8102 Z=0
    g122: LineSegment StartX=306.073 StartY=-62.8351 StartZ=0 EndX=306.073 EndY=-77.8102 EndZ=0
    g123: LineSegment StartX=302.996 StartY=-79.2541 StartZ=0 EndX=236.821 EndY=-24.2775 EndZ=0
    g124: LineSegment StartX=238.538 StartY=-21.7539 StartZ=0 EndX=302.567 EndY=-56.9099 EndZ=0
    g125: Circle CenterX=61.6457 CenterY=-88.8112 CenterZ=0 NormalX=0 NormalY=0 NormalZ=1 AngleXU=0 Radius=1
    g126: Circle CenterX=58.0728 CenterY=-91.7794 CenterZ=0 NormalX=0 NormalY=0 NormalZ=1 AngleXU=0 Radius=1
    g127: Circle CenterX=63.9135 CenterY=-91.7794 CenterZ=0 NormalX=0 NormalY=0 NormalZ=1 AngleXU=0 Radius=1
    g128: BSplineCurve PolesCount=3 KnotsCount=2 Degree=2 IsPeriodic=0
    g129: GeomPoint X=61.6457 Y=-88.8112 Z=0
    g130: GeomPoint X=63.9135 Y=-91.7794 Z=0
    g131: Circle CenterX=179.022 CenterY=-85.8163 CenterZ=0 NormalX=0 NormalY=0 NormalZ=1 AngleXU=0 Radius=1
    g132: Circle CenterX=179.022 CenterY=-91.7794 CenterZ=0 NormalX=0 NormalY=0 NormalZ=1 AngleXU=0 Radius=1
    g133: Circle CenterX=171.895 CenterY=-91.7794 CenterZ=0 NormalX=0 NormalY=0 NormalZ=1 AngleXU=0 Radius=1
    g134: BSplineCurve PolesCount=3 KnotsCount=2 Degree=2 IsPeriodic=0
    g135: GeomPoint X=179.022 Y=-85.8163 Z=0
    g136: GeomPoint X=171.895 Y=-91.7794 Z=0
    g137: Circle CenterX=185.124 CenterY=-86.2028 CenterZ=0 NormalX=0 NormalY=0 NormalZ=1 AngleXU=0 Radius=1
    g138: Circle CenterX=185.124 CenterY=-91.7794 CenterZ=0 NormalX=0 NormalY=0 NormalZ=1 AngleXU=0 Radius=1
    g139: Circle CenterX=191.747 CenterY=-91.7794 CenterZ=0 NormalX=0 NormalY=0 NormalZ=1 AngleXU=0 Radius=1
    g140: BSplineCurve PolesCount=3 KnotsCount=2 Degree=2 IsPeriodic=0
    g141: GeomPoint X=185.124 Y=-86.2028 Z=0
    g142: GeomPoint X=191.747 Y=-91.7794 Z=0
    g143: Circle CenterX=299.888 CenterY=-86.6413 CenterZ=0 NormalX=0 NormalY=0 NormalZ=1 AngleXU=0 Radius=1
    g144: Circle CenterX=306.073 CenterY=-91.7794 CenterZ=0 NormalX=0 NormalY=0 NormalZ=1 AngleXU=0 Radius=1
    g145: Circle CenterX=298.776 CenterY=-91.7794 CenterZ=0 NormalX=0 NormalY=0 NormalZ=1 AngleXU=0 Radius=1
    g146: BSplineCurve PolesCount=3 KnotsCount=2 Degree=2 IsPeriodic=0
    g147: GeomPoint X=299.888 Y=-86.6413 Z=0
    g148: GeomPoint X=298.776 Y=-91.7794 Z=0
    g149: LineSegment StartX=189.124 StartY=5.37834 StartZ=0 EndX=299.888 EndY=-86.6413 EndZ=0
    g150: LineSegment StartX=298.776 StartY=-91.7794 StartZ=0 EndX=191.747 EndY=-91.7794 EndZ=0
    g151: LineSegment StartX=185.124 StartY=-86.2028 StartZ=0 EndX=185.124 EndY=5.34704 EndZ=0
    g152: LineSegment StartX=179.022 StartY=5.34704 StartZ=0 EndX=179.022 EndY=-85.8163 EndZ=0
    g153: LineSegment StartX=171.895 StartY=-91.7794 StartZ=0 EndX=63.9135 EndY=-91.7794 EndZ=0
    g154: LineSegment StartX=61.6457 StartY=-88.8112 StartZ=0 EndX=175.022 EndY=5.37834 EndZ=0
    g155: Circle CenterX=302.073 CenterY=124.221 CenterZ=0 NormalX=0 NormalY=0 NormalZ=1 AngleXU=0 Radius=1
    g156: Circle CenterX=306.073 CenterY=124.221 CenterZ=0 NormalX=0 NormalY=0 NormalZ=1 AngleXU=0 Radius=1
    g157: Circle CenterX=302.996 CenterY=121.665 CenterZ=0 NormalX=0 NormalY=0 NormalZ=1 AngleXU=0 Radius=1
    g158: BSplineCurve PolesCount=3 KnotsCount=2 Degree=2 IsPeriodic=0
    g159: GeomPoint X=302.073 Y=124.221 Z=0
    g160: GeomPoint X=302.996 Y=121.665 Z=0
    g161: Circle CenterX=189.124 CenterY=124.221 CenterZ=0 NormalX=0 NormalY=0 NormalZ=1 AngleXU=0 Radius=1
    g162: Circle CenterX=185.124 CenterY=124.221 CenterZ=0 NormalX=0 NormalY=0 NormalZ=1 AngleXU=0 Radius=1
    g163: Circle CenterX=185.124 CenterY=120.221 CenterZ=0 NormalX=0 NormalY=0 NormalZ=1 AngleXU=0 Radius=1
    g164: BSplineCurve PolesCount=3 KnotsCount=2 Degree=2 IsPeriodic=0
    g165: GeomPoint X=189.124 Y=124.221 Z=0
    g166: GeomPoint X=185.124 Y=120.221 Z=0
    g167: Circle CenterX=175.022 CenterY=124.221 CenterZ=0 NormalX=0 NormalY=0 NormalZ=1 AngleXU=0 Radius=1
    g168: Circle CenterX=179.022 CenterY=124.221 CenterZ=0 NormalX=0 NormalY=0 NormalZ=1 AngleXU=0 Radius=1
    g169: Circle CenterX=179.022 CenterY=120.221 CenterZ=0 NormalX=0 NormalY=0 NormalZ=1 AngleXU=0 Radius=1
    g170: BSplineCurve PolesCount=3 KnotsCount=2 Degree=2 IsPeriodic=0
    g171: GeomPoint X=175.022 Y=124.221 Z=0
    g172: GeomPoint X=179.022 Y=120.221 Z=0
    g173: Circle CenterX=62.0728 CenterY=124.221 CenterZ=0 NormalX=0 NormalY=0 NormalZ=1 AngleXU=0 Radius=1
    g174: Circle CenterX=58.0728 CenterY=124.221 CenterZ=0 NormalX=0 NormalY=0 NormalZ=1 AngleXU=0 Radius=1
    g175: Circle CenterX=61.1496 CenterY=121.665 CenterZ=0 NormalX=0 NormalY=0 NormalZ=1 AngleXU=0 Radius=1
    g176: BSplineCurve PolesCount=3 KnotsCount=2 Degree=2 IsPeriodic=0
    g177: GeomPoint X=62.0728 Y=124.221 Z=0
    g178: GeomPoint X=61.1496 Y=121.665 Z=0
    g179: LineSegment StartX=62.0728 StartY=124.221 StartZ=0 EndX=175.022 EndY=124.221 EndZ=0
    g180: LineSegment StartX=179.022 StartY=120.221 StartZ=0 EndX=179.022 EndY=27.0628 EndZ=0
    g181: LineSegment StartX=185.124 StartY=27.0628 StartZ=0 EndX=185.124 EndY=120.221 EndZ=0
    g182: LineSegment StartX=302.996 StartY=121.665 StartZ=0 EndX=189.124 EndY=27.0628 EndZ=0
    g183: LineSegment StartX=175.022 StartY=27.0628 StartZ=0 EndX=61.1496 EndY=121.665 EndZ=0
    g184: Circle CenterX=61.5791 CenterY=75.4095 CenterZ=0 NormalX=0 NormalY=0 NormalZ=1 AngleXU=0 Radius=1
    g185: Circle CenterX=58.0728 CenterY=77.3346 CenterZ=0 NormalX=0 NormalY=0 NormalZ=1 AngleXU=0 Radius=1
    g186: Circle CenterX=58.0728 CenterY=73.3346 CenterZ=0 NormalX=0 NormalY=0 NormalZ=1 AngleXU=0 Radius=1
    g187: BSplineCurve PolesCount=3 KnotsCount=2 Degree=2 IsPeriodic=0
    g188: GeomPoint X=61.5791 Y=75.4095 Z=0
    g189: GeomPoint X=58.0728 Y=73.3346 Z=0
    g190: Circle CenterX=58.0728 CenterY=-40.8935 CenterZ=0 NormalX=0 NormalY=0 NormalZ=1 AngleXU=0 Radius=1
    g191: Circle CenterX=58.0728 CenterY=-44.8935 CenterZ=0 NormalX=0 NormalY=0 NormalZ=1 AngleXU=0 Radius=1
    g192: Circle CenterX=61.5791 CenterY=-42.9683 CenterZ=0 NormalX=0 NormalY=0 NormalZ=1 AngleXU=0 Radius=1
    g193: BSplineCurve PolesCount=3 KnotsCount=2 Degree=2 IsPeriodic=0
    g194: GeomPoint X=58.0728 Y=-40.8935 Z=0
    g195: GeomPoint X=61.5791 Y=-42.9683 Z=0
    g196: LineSegment StartX=61.5791 StartY=-42.9683 StartZ=0 EndX=165.871 EndY=14.2954 EndZ=0
    g197: LineSegment StartX=165.871 StartY=18.1458 StartZ=0 EndX=61.5791 EndY=75.4095 EndZ=0
    g198: LineSegment StartX=58.0728 StartY=73.3346 StartZ=0 EndX=58.0728 EndY=-40.8935 EndZ=0
    g199: Circle CenterX=302.567 CenterY=-42.9683 CenterZ=0 NormalX=0 NormalY=0 NormalZ=1 AngleXU=0 Radius=1
    g200: Circle CenterX=306.073 CenterY=-44.8935 CenterZ=0 NormalX=0 NormalY=0 NormalZ=1 AngleXU=0 Radius=1
    g201: Circle CenterX=306.073 CenterY=-40.8935 CenterZ=0 NormalX=0 NormalY=0 NormalZ=1 AngleXU=0 Radius=1
    g202: BSplineCurve PolesCount=3 KnotsCount=2 Degree=2 IsPeriodic=0
    g203: GeomPoint X=302.567 Y=-42.9683 Z=0
    g204: GeomPoint X=306.073 Y=-40.8935 Z=0
    g205: Circle CenterX=306.073 CenterY=73.3346 CenterZ=0 NormalX=0 NormalY=0 NormalZ=1 AngleXU=0 Radius=1
    g206: Circle CenterX=306.073 CenterY=77.3346 CenterZ=0 NormalX=0 NormalY=0 NormalZ=1 AngleXU=0 Radius=1
    g207: Circle CenterX=302.567 CenterY=75.4095 CenterZ=0 NormalX=0 NormalY=0 NormalZ=1 AngleXU=0 Radius=1
    g208: BSplineCurve PolesCount=3 KnotsCount=2 Degree=2 IsPeriodic=0
    g209: GeomPoint X=306.073 Y=73.3346 Z=0
    g210: GeomPoint X=302.567 Y=75.4095 Z=0
    g211: LineSegment StartX=302.567 StartY=-42.9683 StartZ=0 EndX=198.275 EndY=14.2954 EndZ=0
    g212: LineSegment StartX=198.275 StartY=18.1458 StartZ=0 EndX=302.567 EndY=75.4095 EndZ=0
    g213: LineSegment StartX=306.073 StartY=73.3346 StartZ=0 EndX=306.073 EndY=-40.8935 EndZ=0
    g214: LineSegment StartX=322.073 StartY=105.865 StartZ=0 EndX=328.643 EndY=105.865 EndZ=0
    g215: LineSegment StartX=318.073 StartY=120.221 StartZ=0 EndX=318.073 EndY=109.865 EndZ=0
    g216: LineSegment StartX=336.157 StartY=107.779 StartZ=0 EndX=362.567 EndY=122.294 EndZ=0
    g217: Circle CenterX=362.073 CenterY=124.221 CenterZ=0 NormalX=0 NormalY=0 NormalZ=1 AngleXU=0 Radius=1
    g218: Circle CenterX=366.073 CenterY=124.221 CenterZ=0 NormalX=0 NormalY=0 NormalZ=1 AngleXU=0 Radius=1
    g219: Circle CenterX=362.567 CenterY=122.294 CenterZ=0 NormalX=0 NormalY=0 NormalZ=1 AngleXU=0 Radius=1
    g220: BSplineCurve PolesCount=3 KnotsCount=2 Degree=2 IsPeriodic=0
    g221: GeomPoint X=362.073 Y=124.221 Z=0
    g222: GeomPoint X=362.567 Y=122.294 Z=0
    g223: Circle CenterX=322.073 CenterY=124.221 CenterZ=0 NormalX=0 NormalY=0 NormalZ=1 AngleXU=0 Radius=1
    g224: Circle CenterX=318.073 CenterY=124.221 CenterZ=0 NormalX=0 NormalY=0 NormalZ=1 AngleXU=0 Radius=1
    g225: Circle CenterX=318.073 CenterY=120.221 CenterZ=0 NormalX=0 NormalY=0 NormalZ=1 AngleXU=0 Radius=1
    g226: BSplineCurve PolesCount=3 KnotsCount=2 Degree=2 IsPeriodic=0
    g227: GeomPoint X=322.073 Y=124.221 Z=0
    g228: GeomPoint X=318.073 Y=120.221 Z=0
    g229: Circle CenterX=322.073 CenterY=105.865 CenterZ=0 NormalX=0 NormalY=0 NormalZ=1 AngleXU=0 Radius=1
    g230: Circle CenterX=318.073 CenterY=105.865 CenterZ=0 NormalX=0 NormalY=0 NormalZ=1 AngleXU=0 Radius=1
    g231: Circle CenterX=318.073 CenterY=109.865 CenterZ=0 NormalX=0 NormalY=0 NormalZ=1 AngleXU=0 Radius=1
    g232: BSplineCurve PolesCount=3 KnotsCount=2 Degree=2 IsPeriodic=0
    g233: GeomPoint X=322.073 Y=105.865 Z=0
    g234: GeomPoint X=318.073 Y=109.865 Z=0
    g235: Circle CenterX=336.157 CenterY=107.779 CenterZ=0 NormalX=0 NormalY=0 NormalZ=1 AngleXU=0 Radius=1
    g236: Circle CenterX=332.651 CenterY=105.853 CenterZ=0 NormalX=0 NormalY=0 NormalZ=1 AngleXU=0 Radius=1
    g237: Circle CenterX=328.643 CenterY=105.865 CenterZ=0 NormalX=0 NormalY=0 NormalZ=1 AngleXU=0 Radius=1
    g238: BSplineCurve PolesCount=3 KnotsCount=2 Degree=2 IsPeriodic=0
    g239: GeomPoint X=336.157 Y=107.779 Z=0
    g240: GeomPoint X=328.643 Y=105.865 Z=0
    g241: LineSegment StartX=322.073 StartY=124.221 StartZ=0 EndX=362.073 EndY=124.221 EndZ=0
    g242: Circle CenterX=371.567 CenterY=-80.8644 CenterZ=0 NormalX=0 NormalY=0 NormalZ=1 AngleXU=0 Radius=1
    g243: Circle CenterX=375.073 CenterY=-82.7896 CenterZ=0 NormalX=0 NormalY=0 NormalZ=1 AngleXU=0 Radius=1
    g244: Circle CenterX=375.073 CenterY=-78.7896 CenterZ=0 NormalX=0 NormalY=0 NormalZ=1 AngleXU=0 Radius=1
    g245: BSplineCurve PolesCount=3 KnotsCount=2 Degree=2 IsPeriodic=0
    g246: GeomPoint X=371.567 Y=-80.8644 Z=0
    g247: GeomPoint X=375.073 Y=-78.7896 Z=0
    g248: Circle CenterX=321.579 CenterY=-53.4075 CenterZ=0 NormalX=0 NormalY=0 NormalZ=1 AngleXU=0 Radius=1
    g249: Circle CenterX=318.073 CenterY=-51.4823 CenterZ=0 NormalX=0 NormalY=0 NormalZ=1 AngleXU=0 Radius=1
    g250: Circle CenterX=318.073 CenterY=-47.4805 CenterZ=0 NormalX=0 NormalY=0 NormalZ=1 AngleXU=0 Radius=1
    g251: BSplineCurve PolesCount=3 KnotsCount=2 Degree=2 IsPeriodic=0
    g252: GeomPoint X=321.579 Y=-53.4075 Z=0
    g253: GeomPoint X=318.073 Y=-47.4805 Z=0
    g254: LineSegment StartX=371.567 StartY=-80.8644 StartZ=0 EndX=321.579 EndY=-53.4075 EndZ=0
    g255: Circle CenterX=321.579 CenterY=-67.3492 CenterZ=0 NormalX=0 NormalY=0 NormalZ=1 AngleXU=0 Radius=1
    g256: Circle CenterX=318.073 CenterY=-65.424 CenterZ=0 NormalX=0 NormalY=0 NormalZ=1 AngleXU=0 Radius=1
    g257: Circle CenterX=318.073 CenterY=-69.424 CenterZ=0 NormalX=0 NormalY=0 NormalZ=1 AngleXU=0 Radius=1
    g258: BSplineCurve PolesCount=3 KnotsCount=2 Degree=2 IsPeriodic=0
    g259: GeomPoint X=321.579 Y=-67.3492 Z=0
    g260: GeomPoint X=318.073 Y=-69.424 Z=0
    g261: Circle CenterX=362.567 CenterY=-89.8542 CenterZ=0 NormalX=0 NormalY=0 NormalZ=1 AngleXU=0 Radius=1
    g262: Circle CenterX=366.073 CenterY=-91.7794 CenterZ=0 NormalX=0 NormalY=0 NormalZ=1 AngleXU=0 Radius=1
    g263: Circle CenterX=362.073 CenterY=-91.7794 CenterZ=0 NormalX=0 NormalY=0 NormalZ=1 AngleXU=0 Radius=1
    g264: BSplineCurve PolesCount=3 KnotsCount=2 Degree=2 IsPeriodic=0
    g265: GeomPoint X=362.567 Y=-89.8542 Z=0
    g266: GeomPoint X=362.073 Y=-91.7794 Z=0
    g267: Circle CenterX=322.073 CenterY=-91.7794 CenterZ=0 NormalX=0 NormalY=0 NormalZ=1 AngleXU=0 Radius=1
    g268: Circle CenterX=318.073 CenterY=-91.7794 CenterZ=0 NormalX=0 NormalY=0 NormalZ=1 AngleXU=0 Radius=1
    g269: Circle CenterX=318.073 CenterY=-87.7794 CenterZ=0 NormalX=0 NormalY=0 NormalZ=1 AngleXU=0 Radius=1
    g270: BSplineCurve PolesCount=3 KnotsCount=2 Degree=2 IsPeriodic=0
    g271: GeomPoint X=322.073 Y=-91.7794 Z=0
    g272: GeomPoint X=318.073 Y=-87.7794 Z=0
    g273: LineSegment StartX=362.567 StartY=-89.8542 StartZ=0 EndX=321.579 EndY=-67.3492 EndZ=0
    g274: LineSegment StartX=318.073 StartY=-69.424 StartZ=0 EndX=318.073 EndY=-87.7794 EndZ=0
    g275: LineSegment StartX=322.073 StartY=-91.7794 StartZ=0 EndX=362.073 EndY=-91.7794 EndZ=0
    g276: Circle CenterX=2.07281 CenterY=124.221 CenterZ=0 NormalX=0 NormalY=0 NormalZ=1 AngleXU=0 Radius=1
    g277: Circle CenterX=1.57905 CenterY=122.295 CenterZ=0 NormalX=0 NormalY=0 NormalZ=1 AngleXU=0 Radius=1
    g278: BSplineCurve PolesCount=3 KnotsCount=2 Degree=2 IsPeriodic=0
    g279: GeomPoint X=2.07281 Y=124.221 Z=0
    g280: GeomPoint X=1.57905 Y=122.295 Z=0
    g281: Circle CenterX=42.0728 CenterY=124.221 CenterZ=0 NormalX=0 NormalY=0 NormalZ=1 AngleXU=0 Radius=1
    g282: Circle CenterX=46.0728 CenterY=124.221 CenterZ=0 NormalX=0 NormalY=0 NormalZ=1 AngleXU=0 Radius=1
    g283: Circle CenterX=46.0728 CenterY=120.221 CenterZ=0 NormalX=0 NormalY=0 NormalZ=1 AngleXU=0 Radius=1
    g284: BSplineCurve PolesCount=3 KnotsCount=2 Degree=2 IsPeriodic=0
    g285: GeomPoint X=42.0728 Y=124.221 Z=0
    g286: GeomPoint X=46.0728 Y=120.221 Z=0
    g287: Circle CenterX=46.0728 CenterY=109.865 CenterZ=0 NormalX=0 NormalY=0 NormalZ=1 AngleXU=0 Radius=1
    g288: Circle CenterX=46.0728 CenterY=105.865 CenterZ=0 NormalX=0 NormalY=0 NormalZ=1 AngleXU=0 Radius=1
    g289: Circle CenterX=42.0728 CenterY=105.865 CenterZ=0 NormalX=0 NormalY=0 NormalZ=1 AngleXU=0 Radius=1
    g290: BSplineCurve PolesCount=3 KnotsCount=2 Degree=2 IsPeriodic=0
    g291: GeomPoint X=46.0728 Y=109.865 Z=0
    g292: GeomPoint X=42.0728 Y=105.865 Z=0
    g293: Circle CenterX=35.5028 CenterY=105.865 CenterZ=0 NormalX=0 NormalY=0 NormalZ=1 AngleXU=0 Radius=1
    g294: Circle CenterX=31.5028 CenterY=105.865 CenterZ=0 NormalX=0 NormalY=0 NormalZ=1 AngleXU=0 Radius=1
    g295: Circle CenterX=27.9965 CenterY=107.79 CenterZ=0 NormalX=0 NormalY=0 NormalZ=1 AngleXU=0 Radius=1
    g296: BSplineCurve PolesCount=3 KnotsCount=2 Degree=2 IsPeriodic=0
    g297: GeomPoint X=35.5028 Y=105.865 Z=0
    g298: GeomPoint X=27.9965 Y=107.79 Z=0
    g299: LineSegment StartX=2.07281 StartY=124.221 StartZ=0 EndX=42.0728 EndY=124.221 EndZ=0
    g300: LineSegment StartX=46.0728 StartY=120.221 StartZ=0 EndX=46.0728 EndY=109.865 EndZ=0
    g301: LineSegment StartX=42.0728 StartY=105.865 StartZ=0 EndX=35.5028 EndY=105.865 EndZ=0
    g302: LineSegment StartX=27.9965 StartY=107.79 StartZ=0 EndX=1.57905 EndY=122.295 EndZ=0
    g303: Circle CenterX=42.5666 CenterY=-67.3492 CenterZ=0 NormalX=0 NormalY=0 NormalZ=1 AngleXU=0 Radius=1
    g304: Circle CenterX=46.0728 CenterY=-65.424 CenterZ=0 NormalX=0 NormalY=0 NormalZ=1 AngleXU=0 Radius=1
    g305: Circle CenterX=46.0728 CenterY=-69.424 CenterZ=0 NormalX=0 NormalY=0 NormalZ=1 AngleXU=0 Radius=1
    g306: BSplineCurve PolesCount=3 KnotsCount=2 Degree=2 IsPeriodic=0
    g307: GeomPoint X=42.5666 Y=-67.3492 Z=0
    g308: GeomPoint X=46.0728 Y=-69.424 Z=0
    g309: Circle CenterX=46.0728 CenterY=-87.7794 CenterZ=0 NormalX=0 NormalY=0 NormalZ=1 AngleXU=0 Radius=1
    g310: Circle CenterX=46.0728 CenterY=-91.7794 CenterZ=0 NormalX=0 NormalY=0 NormalZ=1 AngleXU=0 Radius=1
    g311: Circle CenterX=42.0728 CenterY=-91.7794 CenterZ=0 NormalX=0 NormalY=0 NormalZ=1 AngleXU=0 Radius=1
    g312: BSplineCurve PolesCount=3 KnotsCount=2 Degree=2 IsPeriodic=0
    g313: GeomPoint X=46.0728 Y=-87.7794 Z=0
    g314: GeomPoint X=42.0728 Y=-91.7794 Z=0
    g315: Circle CenterX=2.07281 CenterY=-91.7794 CenterZ=0 NormalX=0 NormalY=0 NormalZ=1 AngleXU=0 Radius=1
    g316: Circle CenterX=-1.92719 CenterY=-91.7794 CenterZ=0 NormalX=0 NormalY=0 NormalZ=1 AngleXU=0 Radius=1
    g317: Circle CenterX=1.57905 CenterY=-89.8542 CenterZ=0 NormalX=0 NormalY=0 NormalZ=1 AngleXU=0 Radius=1
    g318: BSplineCurve PolesCount=3 KnotsCount=2 Degree=2 IsPeriodic=0
    g319: GeomPoint X=2.07281 Y=-91.7794 Z=0
    g320: GeomPoint X=1.57905 Y=-89.8542 Z=0
    g321: LineSegment StartX=2.07281 StartY=-91.7794 StartZ=0 EndX=42.0728 EndY=-91.7794 EndZ=0
    g322: LineSegment StartX=46.0728 StartY=-87.7794 StartZ=0 EndX=46.0728 EndY=-69.424 EndZ=0
    g323: LineSegment StartX=42.5666 StartY=-67.3492 StartZ=0 EndX=1.57905 EndY=-89.8542 EndZ=0
    g324: Circle CenterX=322.073 CenterY=76.4095 CenterZ=0 NormalX=0 NormalY=0 NormalZ=1 AngleXU=0 Radius=4
    g325: BSplineCurve PolesCount=3 KnotsCount=2 Degree=2 IsPeriodic=0
    g326: GeomPoint X=318.073 Y=72.4095 Z=0
    g327: GeomPoint X=322.073 Y=76.4095 Z=0
    g328: Circle CenterX=375.073 CenterY=72.4095 CenterZ=0 NormalX=0 NormalY=0 NormalZ=1 AngleXU=0 Radius=1
    g329: Circle CenterX=375.073 CenterY=76.4095 CenterZ=0 NormalX=0 NormalY=0 NormalZ=1 AngleXU=0 Radius=1
    g330: Circle CenterX=371.073 CenterY=76.4095 CenterZ=0 NormalX=0 NormalY=0 NormalZ=1 AngleXU=0 Radius=1
    g331: BSplineCurve PolesCount=3 KnotsCount=2 Degree=2 IsPeriodic=0
    g332: GeomPoint X=375.073 Y=72.4095 Z=0
    g333: GeomPoint X=371.073 Y=76.4095 Z=0
    g334: LineSegment StartX=322.073 StartY=76.4095 StartZ=0 EndX=371.073 EndY=76.4095 EndZ=0
    g335: LineSegment StartX=318.073 StartY=72.4095 StartZ=0 EndX=318.073 EndY=-47.4805 EndZ=0
    g336: LineSegment StartX=375.073 StartY=72.4095 StartZ=0 EndX=375.073 EndY=-78.7896 EndZ=0
    g337: ArcOfCircle CenterX=-26.9272 CenterY=22.1087 CenterZ=0 NormalX=0 NormalY=0 NormalZ=1 AngleXU=0 Radius=4 StartAngle=5e-16 EndAngle=3.14159
    g338: LineSegment StartX=-22.9272 StartY=22.1087 StartZ=0 EndX=-18.9272 EndY=-83.7794 EndZ=0
    g339: LineSegment StartX=-34.9272 StartY=-83.7794 StartZ=0 EndX=-30.9272 EndY=22.1087 EndZ=0
    g340: ArcOfCircle CenterX=391.073 CenterY=22.1087 CenterZ=0 NormalX=0 NormalY=0 NormalZ=1 AngleXU=0 Radius=4 StartAngle=0 EndAngle=3.14159
    g341: LineSegment StartX=387.073 StartY=22.1087 StartZ=0 EndX=383.073 EndY=-83.7794 EndZ=0
    g342: LineSegment StartX=395.073 StartY=22.1087 StartZ=0 EndX=399.073 EndY=-83.7794 EndZ=0
    g343: Circle CenterX=-10.9272 CenterY=-78.7794 CenterZ=0 NormalX=0 NormalY=0 NormalZ=1 AngleXU=0 Radius=1
    g344: Circle CenterX=-10.9272 CenterY=-82.7794 CenterZ=0 NormalX=0 NormalY=0 NormalZ=1 AngleXU=0 Radius=1
    g345: Circle CenterX=-7.42095 CenterY=-80.8542 CenterZ=0 NormalX=0 NormalY=0 NormalZ=1 AngleXU=0 Radius=1
    g346: BSplineCurve PolesCount=3 KnotsCount=2 Degree=2 IsPeriodic=0
    g347: GeomPoint X=-10.9272 Y=-78.7794 Z=0
    g348: GeomPoint X=-7.42095 Y=-80.8542 Z=0
    g349: Circle CenterX=42.5666 CenterY=-53.4075 CenterZ=0 NormalX=0 NormalY=0 NormalZ=1 AngleXU=0 Radius=1
    g350: Circle CenterX=46.0728 CenterY=-51.4823 CenterZ=0 NormalX=0 NormalY=0 NormalZ=1 AngleXU=0 Radius=1
    g351: Circle CenterX=46.0728 CenterY=-47.4823 CenterZ=0 NormalX=0 NormalY=0 NormalZ=1 AngleXU=0 Radius=1
    g352: BSplineCurve PolesCount=3 KnotsCount=2 Degree=2 IsPeriodic=0
    g353: GeomPoint X=42.5666 Y=-53.4075 Z=0
    g354: GeomPoint X=46.0728 Y=-47.4823 Z=0
    g355: Circle CenterX=46.0728 CenterY=72.4095 CenterZ=0 NormalX=0 NormalY=0 NormalZ=1 AngleXU=0 Radius=1
    g356: Circle CenterX=46.0728 CenterY=76.4095 CenterZ=0 NormalX=0 NormalY=0 NormalZ=1 AngleXU=0 Radius=1
    g357: Circle CenterX=42.0728 CenterY=76.4095 CenterZ=0 NormalX=0 NormalY=0 NormalZ=1 AngleXU=0 Radius=1
    g358: BSplineCurve PolesCount=3 KnotsCount=2 Degree=2 IsPeriodic=0
    g359: GeomPoint X=46.0728 Y=72.4095 Z=0
    g360: GeomPoint X=42.0728 Y=76.4095 Z=0
    g361: Circle CenterX=-6.92718 CenterY=76.4095 CenterZ=0 NormalX=0 NormalY=0 NormalZ=1 AngleXU=0 Radius=1
    g362: Circle CenterX=-10.9272 CenterY=76.4095 CenterZ=0 NormalX=0 NormalY=0 NormalZ=1 AngleXU=0 Radius=1
    g363: Circle CenterX=-10.9272 CenterY=72.4095 CenterZ=0 NormalX=0 NormalY=0 NormalZ=1 AngleXU=0 Radius=1
    g364: BSplineCurve PolesCount=3 KnotsCount=2 Degree=2 IsPeriodic=0
    g365: GeomPoint X=-6.92718 Y=76.4095 Z=0
    g366: GeomPoint X=-10.9272 Y=72.4095 Z=0
    g367: LineSegment StartX=-10.9272 StartY=72.4095 StartZ=0 EndX=-10.9272 EndY=-78.7794 EndZ=0
    g368: LineSegment StartX=-7.42095 StartY=-80.8542 StartZ=0 EndX=42.5666 EndY=-53.4075 EndZ=0
    g369: LineSegment StartX=46.0728 StartY=-47.4823 StartZ=0 EndX=46.0728 EndY=72.4095 EndZ=0
    g370: LineSegment StartX=42.0728 StartY=76.4095 StartZ=0 EndX=-6.92719 EndY=76.4095 EndZ=0
    g371: LineSegment StartX=232.072 StartY=136.221 StartZ=0 EndX=232.072 EndY=-117.815 EndZ=0
    g372: LineSegment StartX=132.072 StartY=136.221 StartZ=0 EndX=132.072 EndY=-121.309 EndZ=0
    g373: LineSegment StartX=245.072 StartY=136.221 StartZ=0 EndX=245.072 EndY=-116.499 EndZ=0
    g374: LineSegment StartX=119.072 StartY=136.221 StartZ=0 EndX=119.072 EndY=-116.228 EndZ=0
    g375: LineSegment StartX=-42.9272 StartY=136.221 StartZ=0 EndX=407.073 EndY=136.221 EndZ=0
    g376: LineSegment StartX=232.072 StartY=136.221 StartZ=0 EndX=220.072 EndY=136.221 EndZ=0
    g377: LineSegment StartX=232.072 StartY=136.221 StartZ=0 EndX=232.072 EndY=124.221 EndZ=0
    g378: LineSegment StartX=220.072 StartY=136.221 StartZ=0 EndX=220.072 EndY=124.221 EndZ=0
    g379: LineSegment StartX=220.072 StartY=136.221 StartZ=0 EndX=226.072 EndY=136.221 EndZ=0
    g380: LineSegment StartX=220.072 StartY=136.221 StartZ=0 EndX=220.072 EndY=130.221 EndZ=0
    g381: LineSegment StartX=220.072 StartY=124.221 StartZ=0 EndX=226.072 EndY=124.221 EndZ=0
    g382: LineSegment StartX=232.072 StartY=124.221 StartZ=0 EndX=232.072 EndY=126.721 EndZ=0
    g383: LineSegment StartX=232.072 StartY=136.221 StartZ=0 EndX=232.072 EndY=133.721 EndZ=0
    g384-g388: Circle x5 (B-spline internal-alignment scaffolding for g389; pole/knot coordinates omitted)
    g389: BSplineCurve PolesCount=5 KnotsCount=3 Degree=3 IsPeriodic=0
    g390: GeomPoint X=232.072 Y=133.721 Z=0
    g391: GeomPoint X=223.072 Y=130.221 Z=0
    g392: GeomPoint X=232.072 Y=126.721 Z=0
  constraints (658):
    c: Vertical(g0)
    c: Vertical(g1)
    c: Block(g1)
    c: Block(g0)
    c: Weight(g4) = 1
    c: Equal(g4,g5)
    c: Equal(g4,g6)
    c: InternalAlignment(g4,g7)
    c: InternalAlignment(g5,g7)
    c: InternalAlignment(g6,g7)
    c: InternalAlignment(g8,g7)
    c: InternalAlignment(g9,g7)
    c: Weight(g10) = 1
    c: Equal(g10,g11)
    c: Equal(g10,g12)
    c: InternalAlignment(g10,g13)
    c: InternalAlignment(g11,g13)
    c: InternalAlignment(g12,g13)
    c: InternalAlignment(g14,g13)
    c: InternalAlignment(g15,g13)
    c: Block(g13)
    c: Block(g7)
    c: Weight(g16) = 1
    c: Equal(g16,g17)
    c: Equal(g16,g18)
    c: InternalAlignment(g16,g19)
    c: InternalAlignment(g17,g19)
    c: InternalAlignment(g18,g19)
    c: InternalAlignment(g20,g19)
    c: InternalAlignment(g21,g19)
    c: Weight(g22) = 1
    c: Equal(g22,g23)
    c: Equal(g22,g24)
    c: InternalAlignment(g22,g25)
    c: InternalAlignment(g23,g25)
    c: InternalAlignment(g24,g25)
    c: InternalAlignment(g26,g25)
    c: InternalAlignment(g27,g25)
    c: Block(g25)
    c: Block(g19)
    c: Weight(g28) = 1
    c: Equal(g28,g29)
    c: Equal(g28,g30)
    c: InternalAlignment(g28,g31)
    c: InternalAlignment(g29,g31)
    c: InternalAlignment(g30,g31)
    c: InternalAlignment(g32,g31)
    c: InternalAlignment(g33,g31)
    c: Weight(g34) = 1
    c: Equal(g34,g35)
    c: Equal(g34,g36)
    c: InternalAlignment(g34,g37)
    c: InternalAlignment(g35,g37)
    c: InternalAlignment(g36,g37)
    c: InternalAlignment(g38,g37)
    c: InternalAlignment(g39,g37)
    c: Block(g31)
    c: Block(g37)
    c: Coincident(g40,g1)
    c: Coincident(g40,g0)
    c: Horizontal(g40)
    c: Distance(g40) = 450
    c: Weight(g41) = 1
    c: Equal(g41,g42)
    c: Equal(g41,g43)
    c: InternalAlignment(g41,g44)
    c: InternalAlignment(g42,g44)
    c: InternalAlignment(g43,g44)
    c: InternalAlignment(g45,g44)
    c: InternalAlignment(g46,g44)
    c: Block(g44)
    c: Weight(g47) = 1
    c: Equal(g47,g48)
    c: Equal(g47,g49)
    c: InternalAlignment(g47,g50)
    c: InternalAlignment(g48,g50)
    c: InternalAlignment(g49,g50)
    c: InternalAlignment(g51,g50)
    c: InternalAlignment(g52,g50)
    c: Block(g50)
    c: Weight(g53) = 1
    c: Equal(g53,g54)
    c: Equal(g53,g55)
    c: InternalAlignment(g53,g56)
    c: InternalAlignment(g54,g56)
    c: InternalAlignment(g55,g56)
    c: InternalAlignment(g57,g56)
    c: InternalAlignment(g58,g56)
    c: Block(g56)
    c: Weight(g59) = 1
    c: Equal(g59,g60)
    c: Equal(g59,g61)
    c: InternalAlignment(g59,g62)
    c: InternalAlignment(g60,g62)
    c: InternalAlignment(g61,g62)
    c: InternalAlignment(g63,g62)
    c: InternalAlignment(g64,g62)
    c: Block(g62)
    c: Weight(g65) = 1
    c: Equal(g65,g66)
    c: Equal(g65,g67)
    c: InternalAlignment(g65,g68)
    c: InternalAlignment(g66,g68)
    c: InternalAlignment(g67,g68)
    c: InternalAlignment(g69,g68)
    c: InternalAlignment(g70,g68)
    c: Weight(g71) = 1
    c: Equal(g71,g72)
    c: Equal(g71,g73)
    c: InternalAlignment(g71,g74)
    c: InternalAlignment(g72,g74)
    c: InternalAlignment(g73,g74)
    c: InternalAlignment(g75,g74)
    c: InternalAlignment(g76,g74)
    c: Block(g68)
    c: Block(g74)
    c: Coincident(g77,g68)
    c: Coincident(g77,g74)
    c: Vertical(g77)
    c: Coincident(g78,g68)
    c: Coincident(g78,g50)
    c: Coincident(g79,g50)
    c: Coincident(g79,g74)
    c: Weight(g80) = 1
    c: Equal(g80,g81)
    c: Equal(g80,g82)
    c: InternalAlignment(g80,g83)
    c: InternalAlignment(g81,g83)
    c: InternalAlignment(g82,g83)
    c: InternalAlignment(g84,g83)
    c: InternalAlignment(g85,g83)
    c: Weight(g86) = 1
    c: Equal(g86,g87)
    c: Equal(g86,g88)
    c: InternalAlignment(g86,g89)
    c: InternalAlignment(g87,g89)
    c: InternalAlignment(g88,g89)
    c: InternalAlignment(g90,g89)
    c: InternalAlignment(g91,g89)
    c: Block(g83)
    c: Block(g89)
    c: Coincident(g92,g83)
    c: Coincident(g92,g89)
    c: Vertical(g92)
    c: Coincident(g93,g83)
    c: Coincident(g93,g44)
    c: Coincident(g94,g44)
    c: Coincident(g94,g89)
    c: Weight(g95) = 1
    c: Equal(g95,g96)
    c: Equal(g95,g97)
    c: InternalAlignment(g95,g98)
    c: InternalAlignment(g96,g98)
    c: InternalAlignment(g97,g98)
    c: InternalAlignment(g99,g98)
    c: InternalAlignment(g100,g98)
    c: Weight(g101) = 1
    c: Equal(g101,g102)
    c: Equal(g101,g103)
    c: InternalAlignment(g101,g104)
    c: InternalAlignment(g102,g104)
    c: InternalAlignment(g103,g104)
    c: InternalAlignment(g105,g104)
    c: InternalAlignment(g106,g104)
    c: Block(g98)
    c: Block(g104)
    c: Coincident(g107,g98)
    c: Coincident(g107,g104)
    c: Vertical(g107)
    c: Coincident(g108,g104)
    c: Coincident(g108,g62)
    c: Coincident(g109,g62)
    c: Coincident(g109,g98)
    c: Weight(g110) = 1
    c: Equal(g110,g111)
    c: Equal(g110,g112)
    c: InternalAlignment(g110,g113)
    c: InternalAlignment(g111,g113)
    c: InternalAlignment(g112,g113)
    c: InternalAlignment(g114,g113)
    c: InternalAlignment(g115,g113)
    c: Weight(g116) = 1
    c: Equal(g116,g117)
    c: Equal(g116,g118)
    c: InternalAlignment(g116,g119)
    c: InternalAlignment(g117,g119)
    c: InternalAlignment(g118,g119)
    c: InternalAlignment(g120,g119)
    c: InternalAlignment(g121,g119)
    c: Block(g113)
    c: Block(g119)
    c: Coincident(g122,g113)
    c: Coincident(g122,g119)
    c: Vertical(g122)
    c: Coincident(g123,g119)
    c: Coincident(g123,g56)
    c: Coincident(g124,g56)
    c: Coincident(g124,g113)
    c: Weight(g125) = 1
    c: Equal(g125,g126)
    c: Equal(g125,g127)
    c: InternalAlignment(g125,g128)
    c: InternalAlignment(g126,g128)
    c: InternalAlignment(g127,g128)
    c: InternalAlignment(g129,g128)
    c: InternalAlignment(g130,g128)
    c: Weight(g131) = 1
    c: Equal(g131,g132)
    c: Equal(g131,g133)
    c: InternalAlignment(g131,g134)
    c: InternalAlignment(g132,g134)
    c: InternalAlignment(g133,g134)
    c: InternalAlignment(g135,g134)
    c: InternalAlignment(g136,g134)
    c: Weight(g137) = 1
    c: Equal(g137,g138)
    c: Equal(g137,g139)
    c: InternalAlignment(g137,g140)
    c: InternalAlignment(g138,g140)
    c: InternalAlignment(g139,g140)
    c: InternalAlignment(g141,g140)
    c: InternalAlignment(g142,g140)
    c: Weight(g143) = 1
    c: Equal(g143,g144)
    c: Equal(g143,g145)
    c: InternalAlignment(g143,g146)
    c: InternalAlignment(g144,g146)
    c: InternalAlignment(g145,g146)
    c: InternalAlignment(g147,g146)
    c: InternalAlignment(g148,g146)
    c: Block(g146)
    c: Block(g140)
    c: Block(g134)
    c: Block(g128)
    c: Coincident(g149,g25)
    c: Coincident(g149,g146)
    c: Coincident(g150,g146)
    c: Coincident(g150,g140)
    c: Horizontal(g150)
    c: Coincident(g151,g140)
    c: Coincident(g151,g25)
    c: Vertical(g151)
    c: Coincident(g152,g19)
    c: Coincident(g152,g134)
    c: Vertical(g152)
    c: Coincident(g153,g134)
    c: Coincident(g153,g128)
    c: Horizontal(g153)
    c: Coincident(g154,g128)
    c: Coincident(g154,g19)
    c: Weight(g155) = 1
    c: Equal(g155,g156)
    c: Equal(g155,g157)
    c: InternalAlignment(g155,g158)
    c: InternalAlignment(g156,g158)
    c: InternalAlignment(g157,g158)
    c: InternalAlignment(g159,g158)
    c: InternalAlignment(g160,g158)
    c: Weight(g161) = 1
    c: Equal(g161,g162)
    c: Equal(g161,g163)
    c: InternalAlignment(g161,g164)
    c: InternalAlignment(g162,g164)
    c: InternalAlignment(g163,g164)
    c: InternalAlignment(g165,g164)
    c: InternalAlignment(g166,g164)
    c: Weight(g167) = 1
    c: Equal(g167,g168)
    c: Equal(g167,g169)
    c: InternalAlignment(g167,g170)
    c: InternalAlignment(g168,g170)
    c: InternalAlignment(g169,g170)
    c: InternalAlignment(g171,g170)
    c: InternalAlignment(g172,g170)
    c: Weight(g173) = 1
    c: Equal(g173,g174)
    c: Equal(g173,g175)
    c: InternalAlignment(g173,g176)
    c: InternalAlignment(g174,g176)
    c: InternalAlignment(g175,g176)
    c: InternalAlignment(g177,g176)
    c: InternalAlignment(g178,g176)
    c: Block(g176)
    c: Block(g170)
    c: Block(g164)
    c: Block(g158)
    c: Coincident(g179,g176)
    c: Coincident(g179,g170)
    c: Horizontal(g179)
    c: Coincident(g180,g170)
    c: Coincident(g180,g7)
    c: Vertical(g180)
    c: Coincident(g181,g13)
    c: Coincident(g181,g164)
    c: Vertical(g181)
    c: Coincident(g182,g158)
    c: Coincident(g182,g13)
    c: Coincident(g183,g7)
    c: Weight(g184) = 1
    c: Equal(g184,g185)
    c: Equal(g184,g186)
    c: InternalAlignment(g184,g187)
    c: InternalAlignment(g185,g187)
    c: InternalAlignment(g186,g187)
    c: InternalAlignment(g188,g187)
    c: InternalAlignment(g189,g187)
    c: Weight(g190) = 1
    c: Equal(g190,g191)
    c: Equal(g190,g192)
    c: InternalAlignment(g190,g193)
    c: InternalAlignment(g191,g193)
    c: InternalAlignment(g192,g193)
    c: InternalAlignment(g194,g193)
    c: InternalAlignment(g195,g193)
    c: Block(g193)
    c: Block(g187)
    c: Coincident(g196,g193)
    c: Coincident(g196,g31)
    c: Coincident(g197,g31)
    c: Coincident(g197,g187)
    c: Coincident(g198,g187)
    c: Coincident(g198,g193)
    c: Vertical(g198)
    c: Weight(g199) = 1
    c: Equal(g199,g200)
    c: Equal(g199,g201)
    c: InternalAlignment(g199,g202)
    c: InternalAlignment(g200,g202)
    c: InternalAlignment(g201,g202)
    c: InternalAlignment(g203,g202)
    c: InternalAlignment(g204,g202)
    c: Weight(g205) = 1
    c: Equal(g205,g206)
    c: Equal(g205,g207)
    c: InternalAlignment(g205,g208)
    c: InternalAlignment(g206,g208)
    c: InternalAlignment(g207,g208)
    c: InternalAlignment(g209,g208)
    c: InternalAlignment(g210,g208)
    c: Block(g208)
    c: Block(g202)
    c: Coincident(g211,g202)
    c: Coincident(g211,g37)
    c: Coincident(g212,g37)
    c: Coincident(g212,g208)
    c: Coincident(g213,g208)
    c: Coincident(g213,g202)
    c: Vertical(g213)
    c: Horizontal(g214)
    c: Block(g214)
    c: Vertical(g215)
    c: Block(g215)
    c: Block(g216)
    c: Weight(g217) = 1
    c: Equal(g217,g218)
    c: Equal(g217,g219)
    c: InternalAlignment(g217,g220)
    c: InternalAlignment(g218,g220)
    c: InternalAlignment(g219,g220)
    c: InternalAlignment(g221,g220)
    c: InternalAlignment(g222,g220)
    c: Weight(g223) = 1
    c: Equal(g223,g224)
    c: Equal(g223,g225)
    c: InternalAlignment(g223,g226)
    c: InternalAlignment(g224,g226)
    c: InternalAlignment(g225,g226)
    c: InternalAlignment(g227,g226)
    c: InternalAlignment(g228,g226)
    c: Weight(g229) = 1
    c: Equal(g229,g230)
    c: Equal(g229,g231)
    c: InternalAlignment(g229,g232)
    c: InternalAlignment(g230,g232)
    c: InternalAlignment(g231,g232)
    c: InternalAlignment(g233,g232)
    c: InternalAlignment(g234,g232)
    c: Weight(g235) = 1
    c: Equal(g235,g236)
    c: Equal(g235,g237)
    c: InternalAlignment(g235,g238)
    c: InternalAlignment(g236,g238)
    c: InternalAlignment(g237,g238)
    c: InternalAlignment(g239,g238)
    c: InternalAlignment(g240,g238)
    c: Block(g220)
    c: Block(g226)
    c: Block(g232)
    c: Block(g238)
    c: Coincident(g241,g226)
    c: Coincident(g241,g220)
    c: Horizontal(g241)
    c: Block(g183)
    c: Weight(g242) = 1
    c: Equal(g242,g243)
    c: Equal(g242,g244)
    c: InternalAlignment(g242,g245)
    c: InternalAlignment(g243,g245)
    c: InternalAlignment(g244,g245)
    c: InternalAlignment(g246,g245)
    c: InternalAlignment(g247,g245)
    c: Weight(g248) = 1
    c: Equal(g248,g249)
    c: Equal(g248,g250)
    c: InternalAlignment(g248,g251)
    c: InternalAlignment(g249,g251)
    c: InternalAlignment(g250,g251)
    c: InternalAlignment(g252,g251)
    c: InternalAlignment(g253,g251)
    c: Block(g245)
    c: Block(g251)
    c: Coincident(g254,g245)
    c: Coincident(g254,g251)
    c: Weight(g255) = 1
    c: Equal(g255,g256)
    c: Equal(g255,g257)
    c: InternalAlignment(g255,g258)
    c: InternalAlignment(g256,g258)
    c: InternalAlignment(g257,g258)
    c: InternalAlignment(g259,g258)
    c: InternalAlignment(g260,g258)
    c: Weight(g261) = 1
    c: Equal(g261,g262)
    c: Equal(g261,g263)
    c: InternalAlignment(g261,g264)
    c: InternalAlignment(g262,g264)
    c: InternalAlignment(g263,g264)
    c: InternalAlignment(g265,g264)
    c: InternalAlignment(g266,g264)
    c: Weight(g267) = 1
    c: Equal(g267,g268)
    c: Equal(g267,g269)
    c: InternalAlignment(g267,g270)
    c: InternalAlignment(g268,g270)
    c: InternalAlignment(g269,g270)
    c: InternalAlignment(g271,g270)
    c: InternalAlignment(g272,g270)
    c: Block(g270)
    c: Block(g264)
    c: Block(g258)
    c: Coincident(g273,g264)
    c: Coincident(g273,g258)
    c: Coincident(g274,g258)
    c: Coincident(g274,g270)
    c: Vertical(g274)
    c: Coincident(g275,g270)
    c: Coincident(g275,g264)
    c: Horizontal(g275)
    c: Weight(g276) = 1
    c: Equal(g276,g277)
    c: InternalAlignment(g276,g278)
    c: InternalAlignment(g277,g278)
    c: InternalAlignment(g279,g278)
    c: InternalAlignment(g280,g278)
    c: Weight(g281) = 1
    c: InternalAlignment(g282,g284)
    c: InternalAlignment(g283,g284)
    c: InternalAlignment(g285,g284)
    c: InternalAlignment(g286,g284)
    c: Weight(g287) = 1
    c: Equal(g287,g288)
    c: Equal(g287,g289)
    c: InternalAlignment(g287,g290)
    c: InternalAlignment(g288,g290)
    c: InternalAlignment(g289,g290)
    c: InternalAlignment(g291,g290)
    c: InternalAlignment(g292,g290)
    c: Equal(g293,g294)
    c: Equal(g293,g295)
    c: InternalAlignment(g293,g296)
    c: InternalAlignment(g294,g296)
    c: InternalAlignment(g295,g296)
    c: InternalAlignment(g297,g296)
    c: InternalAlignment(g298,g296)
    c: Block(g284)
    c: Block(g290)
    c: Block(g296)
    c: Block(g278)
    c: Coincident(g299,g278)
    c: Coincident(g299,g284)
    c: Horizontal(g299)
    c: Coincident(g300,g284)
    c: Coincident(g300,g290)
    c: Vertical(g300)
    c: Coincident(g301,g290)
    c: Coincident(g301,g296)
    c: Horizontal(g301)
    c: Coincident(g302,g296)
    c: Coincident(g302,g278)
    c: Weight(g303) = 1
    c: Equal(g303,g304)
    c: Equal(g303,g305)
    c: InternalAlignment(g303,g306)
    c: InternalAlignment(g304,g306)
    c: InternalAlignment(g305,g306)
    c: InternalAlignment(g307,g306)
    c: InternalAlignment(g308,g306)
    c: Weight(g309) = 1
    c: Equal(g309,g310)
    c: Equal(g309,g311)
    c: InternalAlignment(g309,g312)
    c: InternalAlignment(g310,g312)
    c: InternalAlignment(g311,g312)
    c: InternalAlignment(g313,g312)
    c: InternalAlignment(g314,g312)
    c: Weight(g315) = 1
    c: Equal(g315,g316)
    c: Equal(g315,g317)
    c: InternalAlignment(g315,g318)
    c: InternalAlignment(g316,g318)
    c: InternalAlignment(g317,g318)
    c: InternalAlignment(g319,g318)
    c: InternalAlignment(g320,g318)
    c: Block(g318)
    c: Block(g312)
    c: Block(g306)
    c: Coincident(g321,g318)
    c: Coincident(g321,g312)
    c: Horizontal(g321)
    c: Coincident(g322,g312)
    c: Coincident(g322,g306)
    c: Vertical(g322)
    c: Coincident(g323,g306)
    c: Coincident(g323,g318)
    c: InternalAlignment(g324,g325)
    c: InternalAlignment(g326,g325)
    c: InternalAlignment(g327,g325)
    c: Block(g325)
    c: Equal(g328,g329)
    c: Equal(g328,g330)
    c: InternalAlignment(g328,g331)
    c: InternalAlignment(g329,g331)
    c: InternalAlignment(g330,g331)
    c: InternalAlignment(g332,g331)
    c: InternalAlignment(g333,g331)
    c: Block(g331)
    c: Coincident(g334,g325)
    c: Horizontal(g334)
    c: Block(g334)
    c: Coincident(g335,g325)
    c: Coincident(g335,g251)
    c: Vertical(g335)
    c: Coincident(g336,g331)
    c: Coincident(g336,g245)
    c: Vertical(g336)
    c: Block(g337)
    c: Block(g2)
    c: Distance(g335) = 119.89
    c: Coincident(g338,g337)
    c: Coincident(g338,g2)
    c: Coincident(g339,g2)
    c: Coincident(g339,g337)
    c: Block(g3)
    c: Block(g340)
    c: Coincident(g341,g340)
    c: Coincident(g341,g3)
    c: Coincident(g342,g340)
    c: Coincident(g342,g3)
    c: Block(g342)
    c: Block(g341)
    c: Weight(g343) = 1
    c: Equal(g343,g344)
    c: Equal(g343,g345)
    c: InternalAlignment(g343,g346)
    c: InternalAlignment(g344,g346)
    c: InternalAlignment(g345,g346)
    c: InternalAlignment(g347,g346)
    c: InternalAlignment(g348,g346)
    c: Weight(g349) = 1
    c: Equal(g349,g350)
    c: Equal(g349,g351)
    c: InternalAlignment(g349,g352)
    c: InternalAlignment(g350,g352)
    c: InternalAlignment(g351,g352)
    c: InternalAlignment(g353,g352)
    c: InternalAlignment(g354,g352)
    c: Weight(g355) = 1
    c: Equal(g355,g356)
    c: Equal(g355,g357)
    c: InternalAlignment(g355,g358)
    c: InternalAlignment(g356,g358)
    c: InternalAlignment(g357,g358)
    c: InternalAlignment(g359,g358)
    c: InternalAlignment(g360,g358)
    c: Weight(g361) = 1
    c: Equal(g361,g362)
    c: Equal(g361,g363)
    c: InternalAlignment(g361,g364)
    c: InternalAlignment(g362,g364)
    c: InternalAlignment(g363,g364)
    c: InternalAlignment(g365,g364)
    c: InternalAlignment(g366,g364)
    c: Block(g364)
    c: Block(g358)
    c: Block(g352)
    c: Block(g346)
    c: Coincident(g367,g364)
    c: Coincident(g367,g346)
    c: Vertical(g367)
    c: Coincident(g368,g346)
    c: Coincident(g368,g352)
    c: Coincident(g369,g352)
    c: Coincident(g369,g358)
    c: Vertical(g369)
    c: Coincident(g370,g358)
    c: Coincident(g370,g364)
    c: Horizontal(g370)
    c: Vertical(g371)
    c: Vertical(g372)
    c: Vertical(g373)
    c: Vertical(g374)
    c: Coincident(g375,g0)
    c: Coincident(g375,g1)
    c: Horizontal(g375)
    c: Block(g375)
    c: Distance(g375) = 450
    c: Block(g373)
    c: Block(g371)
    c: Block(g372)
    c: Block(g374)
    c: Distance(g0) = 240
    c: Horizontal(g376)
    c: Distance(g376) = 12
    c: Coincident(g376,g371)
    c: Vertical(g377)
    c: Distance(g377) = 12
    c: Coincident(g377,g371)
    c: Coincident(g378,g376)
    c: Vertical(g378)
    c: Horizontal(g379)
    c: Vertical(g380)
    c: Distance(g380) = 6
    c: Coincident(g380,g376)
    c: Coincident(g379,g376)
    c: Block(g378)
    c: Coincident(g381,g378)
    c: Horizontal(g381)
    c: Distance(g381) = 6
    c: Vertical(g382)
    c: Distance(g382) = 2.5
    c: Coincident(g382,g377)
    c: Vertical(g383)
    c: Distance(g383) = 2.5
    c: Coincident(g383,g371)
    c: Coincident(g389,g383)
    c: Weight(g384) = 1
    c: Equal(g384,g385)
    c: Coincident(g385,g379)
    c: Equal(g384,g386)
    c: Coincident(g386,g380)
    c: Equal(g384,g387)
    c: Coincident(g387,g381)
    c: Equal(g384,g388)
    c: Coincident(g389,g382)
    c: InternalAlignment(g384-g388 -> g389) x5
    c: InternalAlignment(g390,g389)
    c: InternalAlignment(g391,g389)
    c: InternalAlignment(g392,g389)
FEATURE [Part::Extrusion] Extrude005
  Base = -> Sketch003
  Dir = (0,0,1)
  DirMode = 2
  FaceMakerClass = Part::FaceMakerBullseye
  LengthFwd = 24
  LengthRev = 0
  Solid = true
  Symmetric = false
